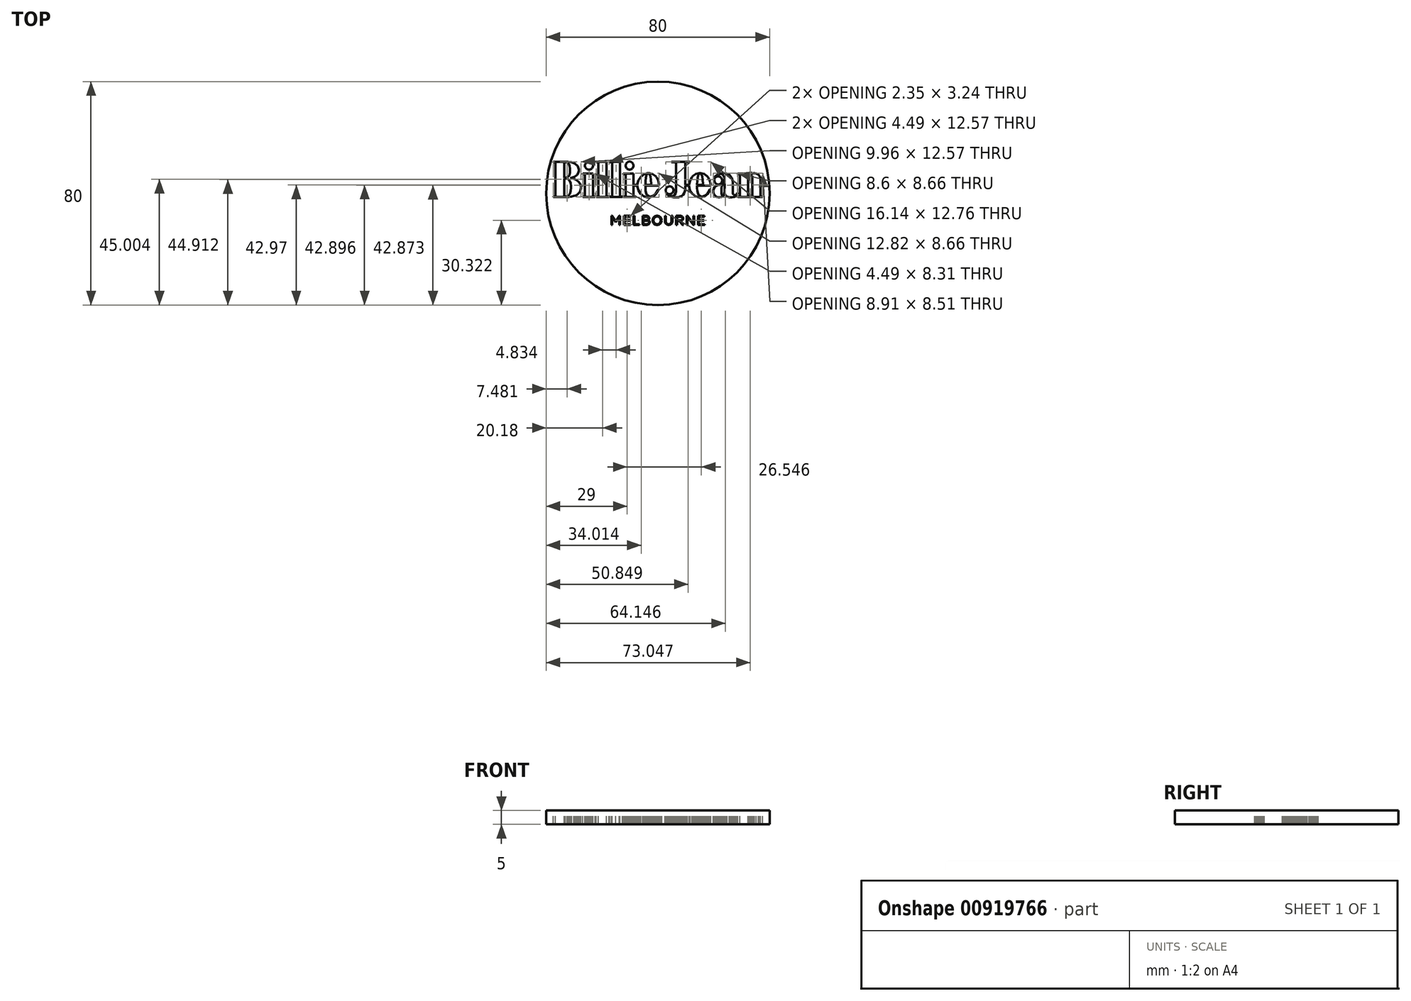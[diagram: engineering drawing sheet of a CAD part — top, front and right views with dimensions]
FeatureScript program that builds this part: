
annotation { "Feature Type Name" : "Feature", "Feature Type Description" : "" }
export const myFeature = defineFeature(function(context is Context, id is Id, definition is map)
    precondition{}
    {
        {
            var Q0;
            Q0=qCreatedBy(makeId("Top.planeOp"),FACE);
            var sketch = newSketch(context, id + "F0", { "sketchPlane" : qUnion([Q0])});
            skLineSegment(sketch, "E0.bottom", {"start": v(40, -20) * mm, "end": v(-40, -20) * mm});
            skLineSegment(sketch, "E0.top", {"start": v(40, 20) * mm, "end": v(-40, 20) * mm});
            skLineSegment(sketch, "E0.left", {"start": v(40, -20) * mm, "end": v(40, 20) * mm});
            skLineSegment(sketch, "E0.right", {"start": v(-40, -20) * mm, "end": v(-40, 20) * mm});
            skPoint(sketch, "E0.middle", {"position": v(0, 0) * mm});
            skCircle(sketch, "E1", {"center": v(0, 0) * mm, "radius": 40 * mm});
            skSolve(sketch);
        }
        {
            var Q0;
            Q0 = qSketchRegion(id + "F0", true);
            extrude(context, id + "F1", {"entities" : qUnion([Q0]), "depth" : 5 * mm, "offsetDistance" : 25 * mm});
        }
        {
            var Q0;
            Q0=makeQuery(id+"F1.opExtrude","CAP_FACE",FACE,{"disambiguationData":[OSD([sQuery(id+"F0.wireOp",EDGE,"E0.bottom"),sQuery(id+"F0.wireOp",EDGE,"E0.top"),sQuery(id+"F0.wireOp",EDGE,"E0.left"),sQuery(id+"F0.wireOp",EDGE,"E0.right")])],"isStart":false});
            var sketch = newSketch(context, id + "F2", { "sketchPlane" : qUnion([Q0])});
            skLineSegment(sketch, "E2", {"start": v(-15.09, -9.91) * mm, "end": v(-16.34, -8.06) * mm});
            skLineSegment(sketch, "E3", {"start": v(-16.34, -8.06) * mm, "end": v(-16.62, -8.06) * mm});
            skLineSegment(sketch, "E4", {"start": v(-16.62, -8.06) * mm, "end": v(-16.62, -11.3) * mm});
            skLineSegment(sketch, "E5", {"start": v(-16.62, -11.3) * mm, "end": v(-16.32, -11.3) * mm});
            skLineSegment(sketch, "E6", {"start": v(-16.32, -11.3) * mm, "end": v(-16.32, -8.61) * mm});
            skLineSegment(sketch, "E7", {"start": v(-16.32, -8.61) * mm, "end": v(-15.13, -10.36) * mm});
            skLineSegment(sketch, "E8", {"start": v(-15.13, -10.36) * mm, "end": v(-15.12, -10.37) * mm});
            skLineSegment(sketch, "E9", {"start": v(-15.12, -10.37) * mm, "end": v(-15.06, -10.37) * mm});
            skLineSegment(sketch, "E10", {"start": v(-15.06, -10.37) * mm, "end": v(-13.86, -8.61) * mm});
            skLineSegment(sketch, "E11", {"start": v(-13.86, -8.61) * mm, "end": v(-13.86, -11.3) * mm});
            skLineSegment(sketch, "E12", {"start": v(-13.86, -11.3) * mm, "end": v(-13.56, -11.3) * mm});
            skLineSegment(sketch, "E13", {"start": v(-13.56, -11.3) * mm, "end": v(-13.56, -8.06) * mm});
            skLineSegment(sketch, "E14", {"start": v(-13.56, -8.06) * mm, "end": v(-13.83, -8.06) * mm});
            skLineSegment(sketch, "E15", {"start": v(-13.83, -8.06) * mm, "end": v(-15.09, -9.91) * mm});
            skLineSegment(sketch, "E16", {"start": v(-11.87, -9.8) * mm, "end": v(-10.05, -9.8) * mm});
            skLineSegment(sketch, "E17", {"start": v(-10.05, -9.8) * mm, "end": v(-10.05, -9.52) * mm});
            skLineSegment(sketch, "E18", {"start": v(-10.05, -9.52) * mm, "end": v(-11.87, -9.52) * mm});
            skLineSegment(sketch, "E19", {"start": v(-11.87, -9.52) * mm, "end": v(-11.87, -8.34) * mm});
            skLineSegment(sketch, "E20", {"start": v(-11.87, -8.34) * mm, "end": v(-9.85, -8.34) * mm});
            skLineSegment(sketch, "E21", {"start": v(-9.85, -8.34) * mm, "end": v(-9.85, -8.06) * mm});
            skLineSegment(sketch, "E22", {"start": v(-9.85, -8.06) * mm, "end": v(-12.17, -8.06) * mm});
            skLineSegment(sketch, "E23", {"start": v(-12.17, -8.06) * mm, "end": v(-12.17, -11.3) * mm});
            skLineSegment(sketch, "E24", {"start": v(-12.17, -11.3) * mm, "end": v(-9.83, -11.3) * mm});
            skLineSegment(sketch, "E25", {"start": v(-9.83, -11.3) * mm, "end": v(-9.83, -11.02) * mm});
            skLineSegment(sketch, "E26", {"start": v(-9.83, -11.02) * mm, "end": v(-11.87, -11.02) * mm});
            skLineSegment(sketch, "E27", {"start": v(-11.87, -11.02) * mm, "end": v(-11.87, -9.8) * mm});
            skLineSegment(sketch, "E28", {"start": v(-8.43, -8.06) * mm, "end": v(-8.73, -8.06) * mm});
            skLineSegment(sketch, "E29", {"start": v(-8.73, -8.06) * mm, "end": v(-8.73, -11.3) * mm});
            skLineSegment(sketch, "E30", {"start": v(-8.73, -11.3) * mm, "end": v(-6.56, -11.3) * mm});
            skLineSegment(sketch, "E31", {"start": v(-6.56, -11.3) * mm, "end": v(-6.56, -11.02) * mm});
            skLineSegment(sketch, "E32", {"start": v(-6.56, -11.02) * mm, "end": v(-8.43, -11.02) * mm});
            skLineSegment(sketch, "E33", {"start": v(-8.43, -11.02) * mm, "end": v(-8.43, -8.06) * mm});
            skLineSegment(sketch, "E34", {"start": v(-5.2, -9.8) * mm, "end": v(-4.15, -9.8) * mm});
            skLineSegment(sketch, "E35", {"start": v(-4.15, -9.8) * mm, "end": v(-3.98, -9.8) * mm});
            skLineSegment(sketch, "E36", {"start": v(-3.98, -9.8) * mm, "end": v(-3.46, -9.96) * mm});
            skLineSegment(sketch, "E37", {"start": v(-3.46, -9.96) * mm, "end": v(-3.22, -10.28) * mm});
            skLineSegment(sketch, "E38", {"start": v(-3.22, -10.28) * mm, "end": v(-3.22, -10.4) * mm});
            skLineSegment(sketch, "E39", {"start": v(-3.22, -10.4) * mm, "end": v(-3.22, -10.4) * mm});
            skLineSegment(sketch, "E40", {"start": v(-3.22, -10.4) * mm, "end": v(-3.22, -10.51) * mm});
            skLineSegment(sketch, "E41", {"start": v(-3.22, -10.51) * mm, "end": v(-3.45, -10.85) * mm});
            skLineSegment(sketch, "E42", {"start": v(-3.45, -10.85) * mm, "end": v(-3.92, -11.02) * mm});
            skLineSegment(sketch, "E43", {"start": v(-3.92, -11.02) * mm, "end": v(-4.07, -11.02) * mm});
            skLineSegment(sketch, "E44", {"start": v(-4.07, -11.02) * mm, "end": v(-5.2, -11.02) * mm});
            skLineSegment(sketch, "E45", {"start": v(-5.2, -11.02) * mm, "end": v(-5.2, -9.8) * mm});
            skLineSegment(sketch, "E46", {"start": v(-4.15, -8.34) * mm, "end": v(-4.01, -8.34) * mm});
            skLineSegment(sketch, "E47", {"start": v(-4.01, -8.34) * mm, "end": v(-3.6, -8.49) * mm});
            skLineSegment(sketch, "E48", {"start": v(-3.6, -8.49) * mm, "end": v(-3.4, -8.8) * mm});
            skLineSegment(sketch, "E49", {"start": v(-3.4, -8.8) * mm, "end": v(-3.4, -8.9) * mm});
            skLineSegment(sketch, "E50", {"start": v(-3.4, -8.9) * mm, "end": v(-3.4, -8.9) * mm});
            skLineSegment(sketch, "E51", {"start": v(-3.4, -8.9) * mm, "end": v(-3.4, -9.02) * mm});
            skLineSegment(sketch, "E52", {"start": v(-3.4, -9.02) * mm, "end": v(-3.6, -9.36) * mm});
            skLineSegment(sketch, "E53", {"start": v(-3.6, -9.36) * mm, "end": v(-4.03, -9.52) * mm});
            skLineSegment(sketch, "E54", {"start": v(-4.03, -9.52) * mm, "end": v(-4.18, -9.52) * mm});
            skLineSegment(sketch, "E55", {"start": v(-4.18, -9.52) * mm, "end": v(-5.2, -9.52) * mm});
            skLineSegment(sketch, "E56", {"start": v(-5.2, -9.52) * mm, "end": v(-5.2, -8.34) * mm});
            skLineSegment(sketch, "E57", {"start": v(-5.2, -8.34) * mm, "end": v(-4.15, -8.34) * mm});
            skLineSegment(sketch, "E58", {"start": v(-3.56, -9.63) * mm, "end": v(-3.5, -9.6) * mm});
            skLineSegment(sketch, "E59", {"start": v(-3.5, -9.6) * mm, "end": v(-3.24, -9.36) * mm});
            skLineSegment(sketch, "E60", {"start": v(-3.24, -9.36) * mm, "end": v(-3.09, -9) * mm});
            skLineSegment(sketch, "E61", {"start": v(-3.09, -9) * mm, "end": v(-3.09, -8.88) * mm});
            skLineSegment(sketch, "E62", {"start": v(-3.09, -8.88) * mm, "end": v(-3.09, -8.87) * mm});
            skLineSegment(sketch, "E63", {"start": v(-3.09, -8.87) * mm, "end": v(-3.09, -8.72) * mm});
            skLineSegment(sketch, "E64", {"start": v(-3.09, -8.72) * mm, "end": v(-3.38, -8.28) * mm});
            skLineSegment(sketch, "E65", {"start": v(-3.38, -8.28) * mm, "end": v(-3.96, -8.06) * mm});
            skLineSegment(sketch, "E66", {"start": v(-3.96, -8.06) * mm, "end": v(-4.15, -8.06) * mm});
            skLineSegment(sketch, "E67", {"start": v(-4.15, -8.06) * mm, "end": v(-5.5, -8.06) * mm});
            skLineSegment(sketch, "E68", {"start": v(-5.5, -8.06) * mm, "end": v(-5.5, -11.3) * mm});
            skLineSegment(sketch, "E69", {"start": v(-5.5, -11.3) * mm, "end": v(-4.08, -11.3) * mm});
            skLineSegment(sketch, "E70", {"start": v(-4.08, -11.3) * mm, "end": v(-3.87, -11.3) * mm});
            skLineSegment(sketch, "E71", {"start": v(-3.87, -11.3) * mm, "end": v(-3.23, -11.05) * mm});
            skLineSegment(sketch, "E72", {"start": v(-3.23, -11.05) * mm, "end": v(-2.9, -10.56) * mm});
            skLineSegment(sketch, "E73", {"start": v(-2.9, -10.56) * mm, "end": v(-2.9, -10.4) * mm});
            skLineSegment(sketch, "E74", {"start": v(-2.9, -10.4) * mm, "end": v(-2.9, -10.4) * mm});
            skLineSegment(sketch, "E75", {"start": v(-2.9, -10.4) * mm, "end": v(-2.9, -10.27) * mm});
            skLineSegment(sketch, "E76", {"start": v(-2.9, -10.27) * mm, "end": v(-3.08, -9.92) * mm});
            skLineSegment(sketch, "E77", {"start": v(-3.08, -9.92) * mm, "end": v(-3.46, -9.66) * mm});
            skLineSegment(sketch, "E78", {"start": v(-3.46, -9.66) * mm, "end": v(-3.56, -9.63) * mm});
            skLineSegment(sketch, "E79", {"start": v(-0.28, -11.07) * mm, "end": v(-0.4, -11.07) * mm});
            skLineSegment(sketch, "E80", {"start": v(-0.4, -11.07) * mm, "end": v(-0.8, -10.97) * mm});
            skLineSegment(sketch, "E81", {"start": v(-0.8, -10.97) * mm, "end": v(-1.22, -10.67) * mm});
            skLineSegment(sketch, "E82", {"start": v(-1.22, -10.67) * mm, "end": v(-1.5, -10.23) * mm});
            skLineSegment(sketch, "E83", {"start": v(-1.5, -10.23) * mm, "end": v(-1.6, -9.81) * mm});
            skLineSegment(sketch, "E84", {"start": v(-1.6, -9.81) * mm, "end": v(-1.6, -9.68) * mm});
            skLineSegment(sketch, "E85", {"start": v(-1.6, -9.68) * mm, "end": v(-1.6, -9.67) * mm});
            skLineSegment(sketch, "E86", {"start": v(-1.6, -9.67) * mm, "end": v(-1.6, -9.53) * mm});
            skLineSegment(sketch, "E87", {"start": v(-1.6, -9.53) * mm, "end": v(-1.5, -9.12) * mm});
            skLineSegment(sketch, "E88", {"start": v(-1.5, -9.12) * mm, "end": v(-1.22, -8.68) * mm});
            skLineSegment(sketch, "E89", {"start": v(-1.22, -8.68) * mm, "end": v(-0.8, -8.39) * mm});
            skLineSegment(sketch, "E90", {"start": v(-0.8, -8.39) * mm, "end": v(-0.42, -8.28) * mm});
            skLineSegment(sketch, "E91", {"start": v(-0.42, -8.28) * mm, "end": v(-0.29, -8.28) * mm});
            skLineSegment(sketch, "E92", {"start": v(-0.29, -8.28) * mm, "end": v(-0.16, -8.28) * mm});
            skLineSegment(sketch, "E93", {"start": v(-0.16, -8.28) * mm, "end": v(0.23, -8.39) * mm});
            skLineSegment(sketch, "E94", {"start": v(0.23, -8.39) * mm, "end": v(0.65, -8.69) * mm});
            skLineSegment(sketch, "E95", {"start": v(0.65, -8.69) * mm, "end": v(0.93, -9.13) * mm});
            skLineSegment(sketch, "E96", {"start": v(0.93, -9.13) * mm, "end": v(1.04, -9.54) * mm});
            skLineSegment(sketch, "E97", {"start": v(1.04, -9.54) * mm, "end": v(1.04, -9.68) * mm});
            skLineSegment(sketch, "E98", {"start": v(1.04, -9.68) * mm, "end": v(1.04, -9.69) * mm});
            skLineSegment(sketch, "E99", {"start": v(1.04, -9.69) * mm, "end": v(1.04, -9.82) * mm});
            skLineSegment(sketch, "E100", {"start": v(1.04, -9.82) * mm, "end": v(0.94, -10.24) * mm});
            skLineSegment(sketch, "E101", {"start": v(0.94, -10.24) * mm, "end": v(0.66, -10.68) * mm});
            skLineSegment(sketch, "E102", {"start": v(0.66, -10.68) * mm, "end": v(0.24, -10.97) * mm});
            skLineSegment(sketch, "E103", {"start": v(0.24, -10.97) * mm, "end": v(-0.15, -11.07) * mm});
            skLineSegment(sketch, "E104", {"start": v(-0.15, -11.07) * mm, "end": v(-0.28, -11.07) * mm});
            skLineSegment(sketch, "E105", {"start": v(1.35, -9.66) * mm, "end": v(1.35, -9.5) * mm});
            skLineSegment(sketch, "E106", {"start": v(1.35, -9.5) * mm, "end": v(1.22, -9) * mm});
            skLineSegment(sketch, "E107", {"start": v(1.22, -9) * mm, "end": v(0.88, -8.47) * mm});
            skLineSegment(sketch, "E108", {"start": v(0.88, -8.47) * mm, "end": v(0.36, -8.13) * mm});
            skLineSegment(sketch, "E109", {"start": v(0.36, -8.13) * mm, "end": v(-0.12, -8) * mm});
            skLineSegment(sketch, "E110", {"start": v(-0.12, -8) * mm, "end": v(-0.28, -8) * mm});
            skLineSegment(sketch, "E111", {"start": v(-0.28, -8) * mm, "end": v(-0.45, -8) * mm});
            skLineSegment(sketch, "E112", {"start": v(-0.45, -8) * mm, "end": v(-0.96, -8.15) * mm});
            skLineSegment(sketch, "E113", {"start": v(-0.96, -8.15) * mm, "end": v(-1.48, -8.53) * mm});
            skLineSegment(sketch, "E114", {"start": v(-1.48, -8.53) * mm, "end": v(-1.8, -9.07) * mm});
            skLineSegment(sketch, "E115", {"start": v(-1.8, -9.07) * mm, "end": v(-1.91, -9.52) * mm});
            skLineSegment(sketch, "E116", {"start": v(-1.91, -9.52) * mm, "end": v(-1.91, -9.68) * mm});
            skLineSegment(sketch, "E117", {"start": v(-1.91, -9.68) * mm, "end": v(-1.91, -9.69) * mm});
            skLineSegment(sketch, "E118", {"start": v(-1.91, -9.69) * mm, "end": v(-1.91, -9.85) * mm});
            skLineSegment(sketch, "E119", {"start": v(-1.91, -9.85) * mm, "end": v(-1.79, -10.35) * mm});
            skLineSegment(sketch, "E120", {"start": v(-1.79, -10.35) * mm, "end": v(-1.45, -10.88) * mm});
            skLineSegment(sketch, "E121", {"start": v(-1.45, -10.88) * mm, "end": v(-0.93, -11.23) * mm});
            skLineSegment(sketch, "E122", {"start": v(-0.93, -11.23) * mm, "end": v(-0.45, -11.35) * mm});
            skLineSegment(sketch, "E123", {"start": v(-0.45, -11.35) * mm, "end": v(-0.29, -11.35) * mm});
            skLineSegment(sketch, "E124", {"start": v(-0.29, -11.35) * mm, "end": v(-0.12, -11.35) * mm});
            skLineSegment(sketch, "E125", {"start": v(-0.12, -11.35) * mm, "end": v(0.4, -11.2) * mm});
            skLineSegment(sketch, "E126", {"start": v(0.4, -11.2) * mm, "end": v(0.91, -10.83) * mm});
            skLineSegment(sketch, "E127", {"start": v(0.91, -10.83) * mm, "end": v(1.23, -10.3) * mm});
            skLineSegment(sketch, "E128", {"start": v(1.23, -10.3) * mm, "end": v(1.35, -9.84) * mm});
            skLineSegment(sketch, "E129", {"start": v(1.35, -9.84) * mm, "end": v(1.35, -9.7) * mm});
            skLineSegment(sketch, "E130", {"start": v(1.35, -9.7) * mm, "end": v(1.35, -9.69) * mm});
            skLineSegment(sketch, "E131", {"start": v(1.35, -9.69) * mm, "end": v(1.35, -9.68) * mm});
            skLineSegment(sketch, "E132", {"start": v(1.35, -9.68) * mm, "end": v(1.35, -9.67) * mm});
            skLineSegment(sketch, "E133", {"start": v(1.35, -9.67) * mm, "end": v(1.35, -9.66) * mm});
            skLineSegment(sketch, "E134", {"start": v(4.89, -9.95) * mm, "end": v(4.89, -10.15) * mm});
            skLineSegment(sketch, "E135", {"start": v(4.89, -10.15) * mm, "end": v(4.62, -10.78) * mm});
            skLineSegment(sketch, "E136", {"start": v(4.62, -10.78) * mm, "end": v(4.05, -11.07) * mm});
            skLineSegment(sketch, "E137", {"start": v(4.05, -11.07) * mm, "end": v(3.86, -11.07) * mm});
            skLineSegment(sketch, "E138", {"start": v(3.86, -11.07) * mm, "end": v(3.67, -11.07) * mm});
            skLineSegment(sketch, "E139", {"start": v(3.67, -11.07) * mm, "end": v(3.1, -10.77) * mm});
            skLineSegment(sketch, "E140", {"start": v(3.1, -10.77) * mm, "end": v(2.82, -10.14) * mm});
            skLineSegment(sketch, "E141", {"start": v(2.82, -10.14) * mm, "end": v(2.82, -9.92) * mm});
            skLineSegment(sketch, "E142", {"start": v(2.82, -9.92) * mm, "end": v(2.82, -8.06) * mm});
            skLineSegment(sketch, "E143", {"start": v(2.82, -8.06) * mm, "end": v(2.52, -8.06) * mm});
            skLineSegment(sketch, "E144", {"start": v(2.52, -8.06) * mm, "end": v(2.52, -9.95) * mm});
            skLineSegment(sketch, "E145", {"start": v(2.52, -9.95) * mm, "end": v(2.52, -10.1) * mm});
            skLineSegment(sketch, "E146", {"start": v(2.52, -10.1) * mm, "end": v(2.6, -10.53) * mm});
            skLineSegment(sketch, "E147", {"start": v(2.6, -10.53) * mm, "end": v(2.88, -10.97) * mm});
            skLineSegment(sketch, "E148", {"start": v(2.88, -10.97) * mm, "end": v(3.3, -11.25) * mm});
            skLineSegment(sketch, "E149", {"start": v(3.3, -11.25) * mm, "end": v(3.71, -11.35) * mm});
            skLineSegment(sketch, "E150", {"start": v(3.71, -11.35) * mm, "end": v(3.85, -11.35) * mm});
            skLineSegment(sketch, "E151", {"start": v(3.85, -11.35) * mm, "end": v(4, -11.35) * mm});
            skLineSegment(sketch, "E152", {"start": v(4, -11.35) * mm, "end": v(4.4, -11.25) * mm});
            skLineSegment(sketch, "E153", {"start": v(4.4, -11.25) * mm, "end": v(4.83, -10.96) * mm});
            skLineSegment(sketch, "E154", {"start": v(4.83, -10.96) * mm, "end": v(5.1, -10.51) * mm});
            skLineSegment(sketch, "E155", {"start": v(5.1, -10.51) * mm, "end": v(5.19, -10.07) * mm});
            skLineSegment(sketch, "E156", {"start": v(5.19, -10.07) * mm, "end": v(5.19, -9.92) * mm});
            skLineSegment(sketch, "E157", {"start": v(5.19, -9.92) * mm, "end": v(5.19, -8.06) * mm});
            skLineSegment(sketch, "E158", {"start": v(5.19, -8.06) * mm, "end": v(4.89, -8.06) * mm});
            skLineSegment(sketch, "E159", {"start": v(4.89, -8.06) * mm, "end": v(4.89, -9.95) * mm});
            skLineSegment(sketch, "E160", {"start": v(6.83, -8.34) * mm, "end": v(7.88, -8.34) * mm});
            skLineSegment(sketch, "E161", {"start": v(7.88, -8.34) * mm, "end": v(8.05, -8.34) * mm});
            skLineSegment(sketch, "E162", {"start": v(8.05, -8.34) * mm, "end": v(8.53, -8.52) * mm});
            skLineSegment(sketch, "E163", {"start": v(8.53, -8.52) * mm, "end": v(8.76, -8.88) * mm});
            skLineSegment(sketch, "E164", {"start": v(8.76, -8.88) * mm, "end": v(8.76, -9) * mm});
            skLineSegment(sketch, "E165", {"start": v(8.76, -9) * mm, "end": v(8.76, -9.01) * mm});
            skLineSegment(sketch, "E166", {"start": v(8.76, -9.01) * mm, "end": v(8.76, -9.14) * mm});
            skLineSegment(sketch, "E167", {"start": v(8.76, -9.14) * mm, "end": v(8.52, -9.52) * mm});
            skLineSegment(sketch, "E168", {"start": v(8.52, -9.52) * mm, "end": v(8.03, -9.7) * mm});
            skLineSegment(sketch, "E169", {"start": v(8.03, -9.7) * mm, "end": v(7.87, -9.7) * mm});
            skLineSegment(sketch, "E170", {"start": v(7.87, -9.7) * mm, "end": v(6.83, -9.7) * mm});
            skLineSegment(sketch, "E171", {"start": v(6.83, -9.7) * mm, "end": v(6.83, -8.34) * mm});
            skLineSegment(sketch, "E172", {"start": v(9.07, -9) * mm, "end": v(9.07, -9) * mm});
            skLineSegment(sketch, "E173", {"start": v(9.07, -9) * mm, "end": v(9.07, -8.82) * mm});
            skLineSegment(sketch, "E174", {"start": v(9.07, -8.82) * mm, "end": v(8.74, -8.31) * mm});
            skLineSegment(sketch, "E175", {"start": v(8.74, -8.31) * mm, "end": v(8.11, -8.06) * mm});
            skLineSegment(sketch, "E176", {"start": v(8.11, -8.06) * mm, "end": v(7.9, -8.06) * mm});
            skLineSegment(sketch, "E177", {"start": v(7.9, -8.06) * mm, "end": v(6.53, -8.06) * mm});
            skLineSegment(sketch, "E178", {"start": v(6.53, -8.06) * mm, "end": v(6.53, -11.3) * mm});
            skLineSegment(sketch, "E179", {"start": v(6.53, -11.3) * mm, "end": v(6.83, -11.3) * mm});
            skLineSegment(sketch, "E180", {"start": v(6.83, -11.3) * mm, "end": v(6.83, -9.98) * mm});
            skLineSegment(sketch, "E181", {"start": v(6.83, -9.98) * mm, "end": v(7.82, -9.98) * mm});
            skLineSegment(sketch, "E182", {"start": v(7.82, -9.98) * mm, "end": v(8.83, -11.3) * mm});
            skLineSegment(sketch, "E183", {"start": v(8.83, -11.3) * mm, "end": v(9.22, -11.3) * mm});
            skLineSegment(sketch, "E184", {"start": v(9.22, -11.3) * mm, "end": v(8.16, -9.93) * mm});
            skLineSegment(sketch, "E185", {"start": v(8.16, -9.93) * mm, "end": v(8.3, -9.91) * mm});
            skLineSegment(sketch, "E186", {"start": v(8.3, -9.91) * mm, "end": v(8.83, -9.62) * mm});
            skLineSegment(sketch, "E187", {"start": v(8.83, -9.62) * mm, "end": v(9.07, -9.16) * mm});
            skLineSegment(sketch, "E188", {"start": v(9.07, -9.16) * mm, "end": v(9.07, -9) * mm});
            skLineSegment(sketch, "E189", {"start": v(12.7, -10.76) * mm, "end": v(10.57, -8.07) * mm});
            skLineSegment(sketch, "E190", {"start": v(10.57, -8.07) * mm, "end": v(10.56, -8.06) * mm});
            skLineSegment(sketch, "E191", {"start": v(10.56, -8.06) * mm, "end": v(10.29, -8.06) * mm});
            skLineSegment(sketch, "E192", {"start": v(10.29, -8.06) * mm, "end": v(10.29, -11.3) * mm});
            skLineSegment(sketch, "E193", {"start": v(10.29, -11.3) * mm, "end": v(10.58, -11.3) * mm});
            skLineSegment(sketch, "E194", {"start": v(10.58, -11.3) * mm, "end": v(10.58, -8.54) * mm});
            skLineSegment(sketch, "E195", {"start": v(10.58, -8.54) * mm, "end": v(12.76, -11.29) * mm});
            skLineSegment(sketch, "E196", {"start": v(12.76, -11.29) * mm, "end": v(12.77, -11.3) * mm});
            skLineSegment(sketch, "E197", {"start": v(12.77, -11.3) * mm, "end": v(13, -11.3) * mm});
            skLineSegment(sketch, "E198", {"start": v(13, -11.3) * mm, "end": v(13, -8.06) * mm});
            skLineSegment(sketch, "E199", {"start": v(13, -8.06) * mm, "end": v(12.7, -8.06) * mm});
            skLineSegment(sketch, "E200", {"start": v(12.7, -8.06) * mm, "end": v(12.7, -10.76) * mm});
            skLineSegment(sketch, "E201", {"start": v(14.67, -11.02) * mm, "end": v(14.67, -9.8) * mm});
            skLineSegment(sketch, "E202", {"start": v(14.67, -9.8) * mm, "end": v(16.5, -9.8) * mm});
            skLineSegment(sketch, "E203", {"start": v(16.5, -9.8) * mm, "end": v(16.5, -9.52) * mm});
            skLineSegment(sketch, "E204", {"start": v(16.5, -9.52) * mm, "end": v(14.67, -9.52) * mm});
            skLineSegment(sketch, "E205", {"start": v(14.67, -9.52) * mm, "end": v(14.67, -8.34) * mm});
            skLineSegment(sketch, "E206", {"start": v(14.67, -8.34) * mm, "end": v(16.7, -8.34) * mm});
            skLineSegment(sketch, "E207", {"start": v(16.7, -8.34) * mm, "end": v(16.7, -8.06) * mm});
            skLineSegment(sketch, "E208", {"start": v(16.7, -8.06) * mm, "end": v(14.37, -8.06) * mm});
            skLineSegment(sketch, "E209", {"start": v(14.37, -8.06) * mm, "end": v(14.37, -11.3) * mm});
            skLineSegment(sketch, "E210", {"start": v(14.37, -11.3) * mm, "end": v(16.72, -11.3) * mm});
            skLineSegment(sketch, "E211", {"start": v(16.72, -11.3) * mm, "end": v(16.72, -11.02) * mm});
            skLineSegment(sketch, "E212", {"start": v(16.72, -11.02) * mm, "end": v(14.67, -11.02) * mm});
            skLineSegment(sketch, "E213", {"start": v(-24.66, 11.35) * mm, "end": v(-24.8, 11.35) * mm});
            skLineSegment(sketch, "E214", {"start": v(-24.8, 11.35) * mm, "end": v(-25.21, 11.24) * mm});
            skLineSegment(sketch, "E215", {"start": v(-25.21, 11.24) * mm, "end": v(-25.67, 10.93) * mm});
            skLineSegment(sketch, "E216", {"start": v(-25.67, 10.93) * mm, "end": v(-25.98, 10.48) * mm});
            skLineSegment(sketch, "E217", {"start": v(-25.98, 10.48) * mm, "end": v(-26.1, 10.06) * mm});
            skLineSegment(sketch, "E218", {"start": v(-26.1, 10.06) * mm, "end": v(-26.1, 9.92) * mm});
            skLineSegment(sketch, "E219", {"start": v(-26.1, 9.92) * mm, "end": v(-26.1, 9.78) * mm});
            skLineSegment(sketch, "E220", {"start": v(-26.1, 9.78) * mm, "end": v(-25.98, 9.36) * mm});
            skLineSegment(sketch, "E221", {"start": v(-25.98, 9.36) * mm, "end": v(-25.67, 8.9) * mm});
            skLineSegment(sketch, "E222", {"start": v(-25.67, 8.9) * mm, "end": v(-25.21, 8.6) * mm});
            skLineSegment(sketch, "E223", {"start": v(-25.21, 8.6) * mm, "end": v(-24.8, 8.48) * mm});
            skLineSegment(sketch, "E224", {"start": v(-24.8, 8.48) * mm, "end": v(-24.66, 8.48) * mm});
            skLineSegment(sketch, "E225", {"start": v(-24.66, 8.48) * mm, "end": v(-24.52, 8.48) * mm});
            skLineSegment(sketch, "E226", {"start": v(-24.52, 8.48) * mm, "end": v(-24.1, 8.6) * mm});
            skLineSegment(sketch, "E227", {"start": v(-24.1, 8.6) * mm, "end": v(-23.64, 8.9) * mm});
            skLineSegment(sketch, "E228", {"start": v(-23.64, 8.9) * mm, "end": v(-23.33, 9.36) * mm});
            skLineSegment(sketch, "E229", {"start": v(-23.33, 9.36) * mm, "end": v(-23.22, 9.78) * mm});
            skLineSegment(sketch, "E230", {"start": v(-23.22, 9.78) * mm, "end": v(-23.22, 9.92) * mm});
            skLineSegment(sketch, "E231", {"start": v(-23.22, 9.92) * mm, "end": v(-23.22, 10.06) * mm});
            skLineSegment(sketch, "E232", {"start": v(-23.22, 10.06) * mm, "end": v(-23.33, 10.48) * mm});
            skLineSegment(sketch, "E233", {"start": v(-23.33, 10.48) * mm, "end": v(-23.64, 10.93) * mm});
            skLineSegment(sketch, "E234", {"start": v(-23.64, 10.93) * mm, "end": v(-24.1, 11.24) * mm});
            skLineSegment(sketch, "E235", {"start": v(-24.1, 11.24) * mm, "end": v(-24.52, 11.35) * mm});
            skLineSegment(sketch, "E236", {"start": v(-24.52, 11.35) * mm, "end": v(-24.66, 11.35) * mm});
            skLineSegment(sketch, "E237", {"start": v(-10.15, 11.35) * mm, "end": v(-10.3, 11.35) * mm});
            skLineSegment(sketch, "E238", {"start": v(-10.3, 11.35) * mm, "end": v(-10.71, 11.24) * mm});
            skLineSegment(sketch, "E239", {"start": v(-10.71, 11.24) * mm, "end": v(-11.17, 10.93) * mm});
            skLineSegment(sketch, "E240", {"start": v(-11.17, 10.93) * mm, "end": v(-11.48, 10.48) * mm});
            skLineSegment(sketch, "E241", {"start": v(-11.48, 10.48) * mm, "end": v(-11.59, 10.06) * mm});
            skLineSegment(sketch, "E242", {"start": v(-11.59, 10.06) * mm, "end": v(-11.59, 9.92) * mm});
            skLineSegment(sketch, "E243", {"start": v(-11.59, 9.92) * mm, "end": v(-11.59, 9.78) * mm});
            skLineSegment(sketch, "E244", {"start": v(-11.59, 9.78) * mm, "end": v(-11.48, 9.36) * mm});
            skLineSegment(sketch, "E245", {"start": v(-11.48, 9.36) * mm, "end": v(-11.17, 8.9) * mm});
            skLineSegment(sketch, "E246", {"start": v(-11.17, 8.9) * mm, "end": v(-10.71, 8.6) * mm});
            skLineSegment(sketch, "E247", {"start": v(-10.71, 8.6) * mm, "end": v(-10.3, 8.48) * mm});
            skLineSegment(sketch, "E248", {"start": v(-10.3, 8.48) * mm, "end": v(-10.15, 8.48) * mm});
            skLineSegment(sketch, "E249", {"start": v(-10.15, 8.48) * mm, "end": v(-10.01, 8.48) * mm});
            skLineSegment(sketch, "E250", {"start": v(-10.01, 8.48) * mm, "end": v(-9.6, 8.6) * mm});
            skLineSegment(sketch, "E251", {"start": v(-9.6, 8.6) * mm, "end": v(-9.14, 8.9) * mm});
            skLineSegment(sketch, "E252", {"start": v(-9.14, 8.9) * mm, "end": v(-8.83, 9.36) * mm});
            skLineSegment(sketch, "E253", {"start": v(-8.83, 9.36) * mm, "end": v(-8.72, 9.78) * mm});
            skLineSegment(sketch, "E254", {"start": v(-8.72, 9.78) * mm, "end": v(-8.72, 9.92) * mm});
            skLineSegment(sketch, "E255", {"start": v(-8.72, 9.92) * mm, "end": v(-8.72, 10.06) * mm});
            skLineSegment(sketch, "E256", {"start": v(-8.72, 10.06) * mm, "end": v(-8.83, 10.48) * mm});
            skLineSegment(sketch, "E257", {"start": v(-8.83, 10.48) * mm, "end": v(-9.14, 10.93) * mm});
            skLineSegment(sketch, "E258", {"start": v(-9.14, 10.93) * mm, "end": v(-9.6, 11.24) * mm});
            skLineSegment(sketch, "E259", {"start": v(-9.6, 11.24) * mm, "end": v(-10.01, 11.35) * mm});
            skLineSegment(sketch, "E260", {"start": v(-10.01, 11.35) * mm, "end": v(-10.15, 11.35) * mm});
            skLineSegment(sketch, "E261", {"start": v(-33.47, 5.51) * mm, "end": v(-33.47, 11.14) * mm});
            skLineSegment(sketch, "E262", {"start": v(-33.47, 11.14) * mm, "end": v(-33.24, 11.14) * mm});
            skLineSegment(sketch, "E263", {"start": v(-33.24, 11.14) * mm, "end": v(-32.55, 10.98) * mm});
            skLineSegment(sketch, "E264", {"start": v(-32.55, 10.98) * mm, "end": v(-31.91, 10.5) * mm});
            skLineSegment(sketch, "E265", {"start": v(-31.91, 10.5) * mm, "end": v(-31.55, 9.7) * mm});
            skLineSegment(sketch, "E266", {"start": v(-31.55, 9.7) * mm, "end": v(-31.43, 8.82) * mm});
            skLineSegment(sketch, "E267", {"start": v(-31.43, 8.82) * mm, "end": v(-31.43, 8.53) * mm});
            skLineSegment(sketch, "E268", {"start": v(-31.43, 8.53) * mm, "end": v(-31.43, 8.22) * mm});
            skLineSegment(sketch, "E269", {"start": v(-31.43, 8.22) * mm, "end": v(-31.48, 7.29) * mm});
            skLineSegment(sketch, "E270", {"start": v(-31.48, 7.29) * mm, "end": v(-31.72, 6.36) * mm});
            skLineSegment(sketch, "E271", {"start": v(-31.72, 6.36) * mm, "end": v(-32.33, 5.76) * mm});
            skLineSegment(sketch, "E272", {"start": v(-32.33, 5.76) * mm, "end": v(-33.19, 5.53) * mm});
            skLineSegment(sketch, "E273", {"start": v(-33.19, 5.53) * mm, "end": v(-33.47, 5.51) * mm});
            skLineSegment(sketch, "E274", {"start": v(-33.47, 5.35) * mm, "end": v(-33.17, 5.35) * mm});
            skLineSegment(sketch, "E275", {"start": v(-33.17, 5.35) * mm, "end": v(-32.27, 5.15) * mm});
            skLineSegment(sketch, "E276", {"start": v(-32.27, 5.15) * mm, "end": v(-31.55, 4.57) * mm});
            skLineSegment(sketch, "E277", {"start": v(-31.55, 4.57) * mm, "end": v(-31.2, 3.63) * mm});
            skLineSegment(sketch, "E278", {"start": v(-31.2, 3.63) * mm, "end": v(-31.11, 2.67) * mm});
            skLineSegment(sketch, "E279", {"start": v(-31.11, 2.67) * mm, "end": v(-31.11, 2.35) * mm});
            skLineSegment(sketch, "E280", {"start": v(-31.11, 2.35) * mm, "end": v(-31.11, 2) * mm});
            skLineSegment(sketch, "E281", {"start": v(-31.11, 2) * mm, "end": v(-31.17, 0.9) * mm});
            skLineSegment(sketch, "E282", {"start": v(-31.17, 0.9) * mm, "end": v(-31.47, -0.18) * mm});
            skLineSegment(sketch, "E283", {"start": v(-31.47, -0.18) * mm, "end": v(-32.18, -0.87) * mm});
            skLineSegment(sketch, "E284", {"start": v(-32.18, -0.87) * mm, "end": v(-33.15, -1.12) * mm});
            skLineSegment(sketch, "E285", {"start": v(-33.15, -1.12) * mm, "end": v(-33.47, -1.12) * mm});
            skLineSegment(sketch, "E286", {"start": v(-33.47, -1.12) * mm, "end": v(-33.47, 5.35) * mm});
            skLineSegment(sketch, "E287", {"start": v(-31.3, 5.45) * mm, "end": v(-30.91, 5.5) * mm});
            skLineSegment(sketch, "E288", {"start": v(-30.91, 5.5) * mm, "end": v(-29.79, 5.9) * mm});
            skLineSegment(sketch, "E289", {"start": v(-29.79, 5.9) * mm, "end": v(-28.87, 6.61) * mm});
            skLineSegment(sketch, "E290", {"start": v(-28.87, 6.61) * mm, "end": v(-28.42, 7.46) * mm});
            skLineSegment(sketch, "E291", {"start": v(-28.42, 7.46) * mm, "end": v(-28.3, 8.1) * mm});
            skLineSegment(sketch, "E292", {"start": v(-28.3, 8.1) * mm, "end": v(-28.3, 8.32) * mm});
            skLineSegment(sketch, "E293", {"start": v(-28.3, 8.32) * mm, "end": v(-28.3, 8.67) * mm});
            skLineSegment(sketch, "E294", {"start": v(-28.3, 8.67) * mm, "end": v(-28.67, 9.7) * mm});
            skLineSegment(sketch, "E295", {"start": v(-28.67, 9.7) * mm, "end": v(-29.65, 10.63) * mm});
            skLineSegment(sketch, "E296", {"start": v(-29.65, 10.63) * mm, "end": v(-31.01, 11.14) * mm});
            skLineSegment(sketch, "E297", {"start": v(-31.01, 11.14) * mm, "end": v(-32.16, 11.3) * mm});
            skLineSegment(sketch, "E298", {"start": v(-32.16, 11.3) * mm, "end": v(-32.54, 11.3) * mm});
            skLineSegment(sketch, "E299", {"start": v(-32.54, 11.3) * mm, "end": v(-37.5, 11.3) * mm});
            skLineSegment(sketch, "E300", {"start": v(-37.5, 11.3) * mm, "end": v(-37.5, 11.14) * mm});
            skLineSegment(sketch, "E301", {"start": v(-37.5, 11.14) * mm, "end": v(-36.7, 11.14) * mm});
            skLineSegment(sketch, "E302", {"start": v(-36.7, 11.14) * mm, "end": v(-36.7, -1.13) * mm});
            skLineSegment(sketch, "E303", {"start": v(-36.7, -1.13) * mm, "end": v(-37.5, -1.13) * mm});
            skLineSegment(sketch, "E304", {"start": v(-37.5, -1.13) * mm, "end": v(-37.5, -1.28) * mm});
            skLineSegment(sketch, "E305", {"start": v(-37.5, -1.28) * mm, "end": v(-32.4, -1.28) * mm});
            skLineSegment(sketch, "E306", {"start": v(-32.4, -1.28) * mm, "end": v(-32.24, -1.28) * mm});
            skLineSegment(sketch, "E307", {"start": v(-32.24, -1.28) * mm, "end": v(-31.77, -1.26) * mm});
            skLineSegment(sketch, "E308", {"start": v(-31.77, -1.26) * mm, "end": v(-30.98, -1.17) * mm});
            skLineSegment(sketch, "E309", {"start": v(-30.98, -1.17) * mm, "end": v(-30.12, -0.97) * mm});
            skLineSegment(sketch, "E310", {"start": v(-30.12, -0.97) * mm, "end": v(-29.46, -0.73) * mm});
            skLineSegment(sketch, "E311", {"start": v(-29.46, -0.73) * mm, "end": v(-29.26, -0.62) * mm});
            skLineSegment(sketch, "E312", {"start": v(-29.26, -0.62) * mm, "end": v(-28.97, -0.48) * mm});
            skLineSegment(sketch, "E313", {"start": v(-28.97, -0.48) * mm, "end": v(-27.97, 0.5) * mm});
            skLineSegment(sketch, "E314", {"start": v(-27.97, 0.5) * mm, "end": v(-27.54, 1.71) * mm});
            skLineSegment(sketch, "E315", {"start": v(-27.54, 1.71) * mm, "end": v(-27.54, 2.11) * mm});
            skLineSegment(sketch, "E316", {"start": v(-27.54, 2.11) * mm, "end": v(-27.54, 2.43) * mm});
            skLineSegment(sketch, "E317", {"start": v(-27.54, 2.43) * mm, "end": v(-27.78, 3.37) * mm});
            skLineSegment(sketch, "E318", {"start": v(-27.78, 3.37) * mm, "end": v(-28.5, 4.36) * mm});
            skLineSegment(sketch, "E319", {"start": v(-28.5, 4.36) * mm, "end": v(-29.69, 5.06) * mm});
            skLineSegment(sketch, "E320", {"start": v(-29.69, 5.06) * mm, "end": v(-30.9, 5.4) * mm});
            skLineSegment(sketch, "E321", {"start": v(-30.9, 5.4) * mm, "end": v(-31.3, 5.45) * mm});
            skLineSegment(sketch, "E322", {"start": v(-23.22, 7.03) * mm, "end": v(-26.9, 7.03) * mm});
            skLineSegment(sketch, "E323", {"start": v(-26.9, 7.03) * mm, "end": v(-26.9, 6.88) * mm});
            skLineSegment(sketch, "E324", {"start": v(-26.9, 6.88) * mm, "end": v(-26.1, 6.88) * mm});
            skLineSegment(sketch, "E325", {"start": v(-26.1, 6.88) * mm, "end": v(-26.1, -1.13) * mm});
            skLineSegment(sketch, "E326", {"start": v(-26.1, -1.13) * mm, "end": v(-26.9, -1.13) * mm});
            skLineSegment(sketch, "E327", {"start": v(-26.9, -1.13) * mm, "end": v(-26.9, -1.28) * mm});
            skLineSegment(sketch, "E328", {"start": v(-26.9, -1.28) * mm, "end": v(-22.4, -1.28) * mm});
            skLineSegment(sketch, "E329", {"start": v(-22.4, -1.28) * mm, "end": v(-22.4, -1.13) * mm});
            skLineSegment(sketch, "E330", {"start": v(-22.4, -1.13) * mm, "end": v(-23.22, -1.13) * mm});
            skLineSegment(sketch, "E331", {"start": v(-23.22, -1.13) * mm, "end": v(-23.22, 7.03) * mm});
            skLineSegment(sketch, "E332", {"start": v(-18.39, 11.3) * mm, "end": v(-22.07, 11.3) * mm});
            skLineSegment(sketch, "E333", {"start": v(-22.07, 11.3) * mm, "end": v(-22.07, 11.14) * mm});
            skLineSegment(sketch, "E334", {"start": v(-22.07, 11.14) * mm, "end": v(-21.26, 11.14) * mm});
            skLineSegment(sketch, "E335", {"start": v(-21.26, 11.14) * mm, "end": v(-21.26, -1.13) * mm});
            skLineSegment(sketch, "E336", {"start": v(-21.26, -1.13) * mm, "end": v(-22.07, -1.13) * mm});
            skLineSegment(sketch, "E337", {"start": v(-22.07, -1.13) * mm, "end": v(-22.07, -1.28) * mm});
            skLineSegment(sketch, "E338", {"start": v(-22.07, -1.28) * mm, "end": v(-17.57, -1.28) * mm});
            skLineSegment(sketch, "E339", {"start": v(-17.57, -1.28) * mm, "end": v(-17.57, -1.13) * mm});
            skLineSegment(sketch, "E340", {"start": v(-17.57, -1.13) * mm, "end": v(-18.39, -1.13) * mm});
            skLineSegment(sketch, "E341", {"start": v(-18.39, -1.13) * mm, "end": v(-18.39, 11.3) * mm});
            skLineSegment(sketch, "E342", {"start": v(-13.55, 11.3) * mm, "end": v(-17.23, 11.3) * mm});
            skLineSegment(sketch, "E343", {"start": v(-17.23, 11.3) * mm, "end": v(-17.23, 11.14) * mm});
            skLineSegment(sketch, "E344", {"start": v(-17.23, 11.14) * mm, "end": v(-16.42, 11.14) * mm});
            skLineSegment(sketch, "E345", {"start": v(-16.42, 11.14) * mm, "end": v(-16.42, -1.13) * mm});
            skLineSegment(sketch, "E346", {"start": v(-16.42, -1.13) * mm, "end": v(-17.23, -1.13) * mm});
            skLineSegment(sketch, "E347", {"start": v(-17.23, -1.13) * mm, "end": v(-17.23, -1.28) * mm});
            skLineSegment(sketch, "E348", {"start": v(-17.23, -1.28) * mm, "end": v(-12.74, -1.28) * mm});
            skLineSegment(sketch, "E349", {"start": v(-12.74, -1.28) * mm, "end": v(-12.74, -1.13) * mm});
            skLineSegment(sketch, "E350", {"start": v(-12.74, -1.13) * mm, "end": v(-13.55, -1.13) * mm});
            skLineSegment(sketch, "E351", {"start": v(-13.55, -1.13) * mm, "end": v(-13.55, 11.3) * mm});
            skLineSegment(sketch, "E352", {"start": v(-3.46, 7.07) * mm, "end": v(-3.45, 7.07) * mm});
            skLineSegment(sketch, "E353", {"start": v(-3.45, 7.07) * mm, "end": v(-3.33, 7.07) * mm});
            skLineSegment(sketch, "E354", {"start": v(-3.33, 7.07) * mm, "end": v(-2.99, 6.8) * mm});
            skLineSegment(sketch, "E355", {"start": v(-2.99, 6.8) * mm, "end": v(-2.67, 6.05) * mm});
            skLineSegment(sketch, "E356", {"start": v(-2.67, 6.05) * mm, "end": v(-2.48, 4.79) * mm});
            skLineSegment(sketch, "E357", {"start": v(-2.48, 4.79) * mm, "end": v(-2.41, 3.43) * mm});
            skLineSegment(sketch, "E358", {"start": v(-2.41, 3.43) * mm, "end": v(-2.4, 2.97) * mm});
            skLineSegment(sketch, "E359", {"start": v(-2.4, 2.97) * mm, "end": v(-4.48, 2.97) * mm});
            skLineSegment(sketch, "E360", {"start": v(-4.48, 2.97) * mm, "end": v(-4.48, 3.32) * mm});
            skLineSegment(sketch, "E361", {"start": v(-4.48, 3.32) * mm, "end": v(-4.44, 4.34) * mm});
            skLineSegment(sketch, "E362", {"start": v(-4.44, 4.34) * mm, "end": v(-4.3, 5.65) * mm});
            skLineSegment(sketch, "E363", {"start": v(-4.3, 5.65) * mm, "end": v(-4, 6.65) * mm});
            skLineSegment(sketch, "E364", {"start": v(-4, 6.65) * mm, "end": v(-3.6, 7.06) * mm});
            skLineSegment(sketch, "E365", {"start": v(-3.6, 7.06) * mm, "end": v(-3.46, 7.07) * mm});
            skLineSegment(sketch, "E366", {"start": v(0.43, 2.79) * mm, "end": v(0.43, 2.95) * mm});
            skLineSegment(sketch, "E367", {"start": v(0.43, 2.95) * mm, "end": v(0.42, 3.24) * mm});
            skLineSegment(sketch, "E368", {"start": v(0.42, 3.24) * mm, "end": v(0.11, 4.6) * mm});
            skLineSegment(sketch, "E369", {"start": v(0.11, 4.6) * mm, "end": v(-0.54, 5.79) * mm});
            skLineSegment(sketch, "E370", {"start": v(-0.54, 5.79) * mm, "end": v(-0.72, 5.99) * mm});
            skLineSegment(sketch, "E371", {"start": v(-0.72, 5.99) * mm, "end": v(-0.9, 6.19) * mm});
            skLineSegment(sketch, "E372", {"start": v(-0.9, 6.19) * mm, "end": v(-1.96, 6.9) * mm});
            skLineSegment(sketch, "E373", {"start": v(-1.96, 6.9) * mm, "end": v(-3.07, 7.22) * mm});
            skLineSegment(sketch, "E374", {"start": v(-3.07, 7.22) * mm, "end": v(-3.44, 7.22) * mm});
            skLineSegment(sketch, "E375", {"start": v(-3.44, 7.22) * mm, "end": v(-3.81, 7.22) * mm});
            skLineSegment(sketch, "E376", {"start": v(-3.81, 7.22) * mm, "end": v(-4.93, 6.9) * mm});
            skLineSegment(sketch, "E377", {"start": v(-4.93, 6.9) * mm, "end": v(-6.14, 6) * mm});
            skLineSegment(sketch, "E378", {"start": v(-6.14, 6) * mm, "end": v(-6.97, 4.64) * mm});
            skLineSegment(sketch, "E379", {"start": v(-6.97, 4.64) * mm, "end": v(-7.3, 3.4) * mm});
            skLineSegment(sketch, "E380", {"start": v(-7.3, 3.4) * mm, "end": v(-7.3, 2.97) * mm});
            skLineSegment(sketch, "E381", {"start": v(-7.3, 2.97) * mm, "end": v(-8.72, 2.97) * mm});
            skLineSegment(sketch, "E382", {"start": v(-8.72, 2.97) * mm, "end": v(-8.72, 7.03) * mm});
            skLineSegment(sketch, "E383", {"start": v(-8.72, 7.03) * mm, "end": v(-12.4, 7.03) * mm});
            skLineSegment(sketch, "E384", {"start": v(-12.4, 7.03) * mm, "end": v(-12.4, 6.88) * mm});
            skLineSegment(sketch, "E385", {"start": v(-12.4, 6.88) * mm, "end": v(-11.59, 6.88) * mm});
            skLineSegment(sketch, "E386", {"start": v(-11.59, 6.88) * mm, "end": v(-11.59, -1.13) * mm});
            skLineSegment(sketch, "E387", {"start": v(-11.59, -1.13) * mm, "end": v(-12.4, -1.13) * mm});
            skLineSegment(sketch, "E388", {"start": v(-12.4, -1.13) * mm, "end": v(-12.4, -1.28) * mm});
            skLineSegment(sketch, "E389", {"start": v(-12.4, -1.28) * mm, "end": v(-7.9, -1.28) * mm});
            skLineSegment(sketch, "E390", {"start": v(-7.9, -1.28) * mm, "end": v(-7.9, -1.13) * mm});
            skLineSegment(sketch, "E391", {"start": v(-7.9, -1.13) * mm, "end": v(-8.72, -1.13) * mm});
            skLineSegment(sketch, "E392", {"start": v(-8.72, -1.13) * mm, "end": v(-8.72, 2.79) * mm});
            skLineSegment(sketch, "E393", {"start": v(-8.72, 2.79) * mm, "end": v(-7.3, 2.79) * mm});
            skLineSegment(sketch, "E394", {"start": v(-7.3, 2.79) * mm, "end": v(-7.3, 2.38) * mm});
            skLineSegment(sketch, "E395", {"start": v(-7.3, 2.38) * mm, "end": v(-7, 1.17) * mm});
            skLineSegment(sketch, "E396", {"start": v(-7, 1.17) * mm, "end": v(-6.2, -0.16) * mm});
            skLineSegment(sketch, "E397", {"start": v(-6.2, -0.16) * mm, "end": v(-5.02, -1.07) * mm});
            skLineSegment(sketch, "E398", {"start": v(-5.02, -1.07) * mm, "end": v(-3.93, -1.42) * mm});
            skLineSegment(sketch, "E399", {"start": v(-3.93, -1.42) * mm, "end": v(-3.57, -1.43) * mm});
            skLineSegment(sketch, "E400", {"start": v(-3.57, -1.43) * mm, "end": v(-3.49, -1.43) * mm});
            skLineSegment(sketch, "E401", {"start": v(-3.49, -1.43) * mm, "end": v(-3.24, -1.42) * mm});
            skLineSegment(sketch, "E402", {"start": v(-3.24, -1.42) * mm, "end": v(-2.8, -1.36) * mm});
            skLineSegment(sketch, "E403", {"start": v(-2.8, -1.36) * mm, "end": v(-2.28, -1.22) * mm});
            skLineSegment(sketch, "E404", {"start": v(-2.28, -1.22) * mm, "end": v(-1.72, -1) * mm});
            skLineSegment(sketch, "E405", {"start": v(-1.72, -1) * mm, "end": v(-1.15, -0.63) * mm});
            skLineSegment(sketch, "E406", {"start": v(-1.15, -0.63) * mm, "end": v(-0.61, -0.13) * mm});
            skLineSegment(sketch, "E407", {"start": v(-0.61, -0.13) * mm, "end": v(-0.14, 0.56) * mm});
            skLineSegment(sketch, "E408", {"start": v(-0.14, 0.56) * mm, "end": v(0.16, 1.22) * mm});
            skLineSegment(sketch, "E409", {"start": v(0.16, 1.22) * mm, "end": v(0.24, 1.45) * mm});
            skLineSegment(sketch, "E410", {"start": v(0.24, 1.45) * mm, "end": v(0.25, 1.52) * mm});
            skLineSegment(sketch, "E411", {"start": v(0.25, 1.52) * mm, "end": v(0.1, 1.52) * mm});
            skLineSegment(sketch, "E412", {"start": v(0.1, 1.52) * mm, "end": v(-0.02, 1.2) * mm});
            skLineSegment(sketch, "E413", {"start": v(-0.02, 1.2) * mm, "end": v(-0.1, 0.97) * mm});
            skLineSegment(sketch, "E414", {"start": v(-0.1, 0.97) * mm, "end": v(-0.74, 0) * mm});
            skLineSegment(sketch, "E415", {"start": v(-0.74, 0) * mm, "end": v(-1.6, -0.74) * mm});
            skLineSegment(sketch, "E416", {"start": v(-1.6, -0.74) * mm, "end": v(-1.8, -0.85) * mm});
            skLineSegment(sketch, "E417", {"start": v(-1.8, -0.85) * mm, "end": v(-1.9, -0.9) * mm});
            skLineSegment(sketch, "E418", {"start": v(-1.9, -0.9) * mm, "end": v(-2.64, -1.13) * mm});
            skLineSegment(sketch, "E419", {"start": v(-2.64, -1.13) * mm, "end": v(-2.88, -1.13) * mm});
            skLineSegment(sketch, "E420", {"start": v(-2.88, -1.13) * mm, "end": v(-3.1, -1.13) * mm});
            skLineSegment(sketch, "E421", {"start": v(-3.1, -1.13) * mm, "end": v(-3.69, -0.84) * mm});
            skLineSegment(sketch, "E422", {"start": v(-3.69, -0.84) * mm, "end": v(-3.74, -0.78) * mm});
            skLineSegment(sketch, "E423", {"start": v(-3.74, -0.78) * mm, "end": v(-3.89, -0.64) * mm});
            skLineSegment(sketch, "E424", {"start": v(-3.89, -0.64) * mm, "end": v(-4.17, -0.06) * mm});
            skLineSegment(sketch, "E425", {"start": v(-4.17, -0.06) * mm, "end": v(-4.39, 0.88) * mm});
            skLineSegment(sketch, "E426", {"start": v(-4.39, 0.88) * mm, "end": v(-4.47, 1.88) * mm});
            skLineSegment(sketch, "E427", {"start": v(-4.47, 1.88) * mm, "end": v(-4.48, 2.56) * mm});
            skLineSegment(sketch, "E428", {"start": v(-4.48, 2.56) * mm, "end": v(-4.48, 2.79) * mm});
            skLineSegment(sketch, "E429", {"start": v(-4.48, 2.79) * mm, "end": v(0.43, 2.79) * mm});
            skLineSegment(sketch, "E430", {"start": v(-37.5, -9.57) * mm, "end": v(-37.5, -9.75) * mm});
            skLineSegment(sketch, "E431", {"start": v(-37.5, -9.75) * mm, "end": v(-19.8, -9.75) * mm});
            skLineSegment(sketch, "E432", {"start": v(-19.8, -9.75) * mm, "end": v(-19.8, -9.57) * mm});
            skLineSegment(sketch, "E433", {"start": v(-19.8, -9.57) * mm, "end": v(-37.5, -9.57) * mm});
            skLineSegment(sketch, "E434", {"start": v(19.8, -9.57) * mm, "end": v(19.8, -9.75) * mm});
            skLineSegment(sketch, "E435", {"start": v(19.8, -9.75) * mm, "end": v(37.5, -9.75) * mm});
            skLineSegment(sketch, "E436", {"start": v(37.5, -9.75) * mm, "end": v(37.5, -9.57) * mm});
            skLineSegment(sketch, "E437", {"start": v(37.5, -9.57) * mm, "end": v(19.8, -9.57) * mm});
            skLineSegment(sketch, "E438", {"start": v(15.03, 7.07) * mm, "end": v(15.05, 7.07) * mm});
            skLineSegment(sketch, "E439", {"start": v(15.05, 7.07) * mm, "end": v(15.17, 7.07) * mm});
            skLineSegment(sketch, "E440", {"start": v(15.17, 7.07) * mm, "end": v(15.5, 6.8) * mm});
            skLineSegment(sketch, "E441", {"start": v(15.5, 6.8) * mm, "end": v(15.83, 6.05) * mm});
            skLineSegment(sketch, "E442", {"start": v(15.83, 6.05) * mm, "end": v(16.02, 4.79) * mm});
            skLineSegment(sketch, "E443", {"start": v(16.02, 4.79) * mm, "end": v(16.08, 3.43) * mm});
            skLineSegment(sketch, "E444", {"start": v(16.08, 3.43) * mm, "end": v(16.08, 2.97) * mm});
            skLineSegment(sketch, "E445", {"start": v(16.08, 2.97) * mm, "end": v(14.02, 2.97) * mm});
            skLineSegment(sketch, "E446", {"start": v(14.02, 2.97) * mm, "end": v(14.02, 3.32) * mm});
            skLineSegment(sketch, "E447", {"start": v(14.02, 3.32) * mm, "end": v(14.05, 4.34) * mm});
            skLineSegment(sketch, "E448", {"start": v(14.05, 4.34) * mm, "end": v(14.2, 5.65) * mm});
            skLineSegment(sketch, "E449", {"start": v(14.2, 5.65) * mm, "end": v(14.5, 6.65) * mm});
            skLineSegment(sketch, "E450", {"start": v(14.5, 6.65) * mm, "end": v(14.9, 7.06) * mm});
            skLineSegment(sketch, "E451", {"start": v(14.9, 7.06) * mm, "end": v(15.03, 7.07) * mm});
            skLineSegment(sketch, "E452", {"start": v(18.92, 2.79) * mm, "end": v(18.92, 2.95) * mm});
            skLineSegment(sketch, "E453", {"start": v(18.92, 2.95) * mm, "end": v(18.91, 3.24) * mm});
            skLineSegment(sketch, "E454", {"start": v(18.91, 3.24) * mm, "end": v(18.6, 4.6) * mm});
            skLineSegment(sketch, "E455", {"start": v(18.6, 4.6) * mm, "end": v(17.95, 5.79) * mm});
            skLineSegment(sketch, "E456", {"start": v(17.95, 5.79) * mm, "end": v(17.77, 5.99) * mm});
            skLineSegment(sketch, "E457", {"start": v(17.77, 5.99) * mm, "end": v(17.6, 6.19) * mm});
            skLineSegment(sketch, "E458", {"start": v(17.6, 6.19) * mm, "end": v(16.53, 6.9) * mm});
            skLineSegment(sketch, "E459", {"start": v(16.53, 6.9) * mm, "end": v(15.42, 7.22) * mm});
            skLineSegment(sketch, "E460", {"start": v(15.42, 7.22) * mm, "end": v(15.06, 7.22) * mm});
            skLineSegment(sketch, "E461", {"start": v(15.06, 7.22) * mm, "end": v(14.69, 7.22) * mm});
            skLineSegment(sketch, "E462", {"start": v(14.69, 7.22) * mm, "end": v(13.58, 6.9) * mm});
            skLineSegment(sketch, "E463", {"start": v(13.58, 6.9) * mm, "end": v(12.52, 6.19) * mm});
            skLineSegment(sketch, "E464", {"start": v(12.52, 6.19) * mm, "end": v(12.34, 5.99) * mm});
            skLineSegment(sketch, "E465", {"start": v(12.34, 5.99) * mm, "end": v(12.16, 5.8) * mm});
            skLineSegment(sketch, "E466", {"start": v(12.16, 5.8) * mm, "end": v(11.5, 4.62) * mm});
            skLineSegment(sketch, "E467", {"start": v(11.5, 4.62) * mm, "end": v(11.2, 3.26) * mm});
            skLineSegment(sketch, "E468", {"start": v(11.2, 3.26) * mm, "end": v(11.2, 2.97) * mm});
            skLineSegment(sketch, "E469", {"start": v(11.2, 2.97) * mm, "end": v(9.75, 2.97) * mm});
            skLineSegment(sketch, "E470", {"start": v(9.75, 2.97) * mm, "end": v(9.75, 11.14) * mm});
            skLineSegment(sketch, "E471", {"start": v(9.75, 11.14) * mm, "end": v(11.4, 11.14) * mm});
            skLineSegment(sketch, "E472", {"start": v(11.4, 11.14) * mm, "end": v(11.4, 11.3) * mm});
            skLineSegment(sketch, "E473", {"start": v(11.4, 11.3) * mm, "end": v(4.9, 11.3) * mm});
            skLineSegment(sketch, "E474", {"start": v(4.9, 11.3) * mm, "end": v(4.9, 11.14) * mm});
            skLineSegment(sketch, "E475", {"start": v(4.9, 11.14) * mm, "end": v(6.54, 11.14) * mm});
            skLineSegment(sketch, "E476", {"start": v(6.54, 11.14) * mm, "end": v(6.54, 0.95) * mm});
            skLineSegment(sketch, "E477", {"start": v(6.54, 0.95) * mm, "end": v(6.54, 0.73) * mm});
            skLineSegment(sketch, "E478", {"start": v(6.54, 0.73) * mm, "end": v(6.4, 0.08) * mm});
            skLineSegment(sketch, "E479", {"start": v(6.4, 0.08) * mm, "end": v(6.01, -0.52) * mm});
            skLineSegment(sketch, "E480", {"start": v(6.01, -0.52) * mm, "end": v(5.48, -0.88) * mm});
            skLineSegment(sketch, "E481", {"start": v(5.48, -0.88) * mm, "end": v(5.04, -1) * mm});
            skLineSegment(sketch, "E482", {"start": v(5.04, -1) * mm, "end": v(4.89, -1) * mm});
            skLineSegment(sketch, "E483", {"start": v(4.89, -1) * mm, "end": v(4.66, -1) * mm});
            skLineSegment(sketch, "E484", {"start": v(4.66, -1) * mm, "end": v(3.96, -0.72) * mm});
            skLineSegment(sketch, "E485", {"start": v(3.96, -0.72) * mm, "end": v(3.34, -0.13) * mm});
            skLineSegment(sketch, "E486", {"start": v(3.34, -0.13) * mm, "end": v(3.25, 0.03) * mm});
            skLineSegment(sketch, "E487", {"start": v(3.25, 0.03) * mm, "end": v(3.32, -0.03) * mm});
            skLineSegment(sketch, "E488", {"start": v(3.32, -0.03) * mm, "end": v(3.99, -0.32) * mm});
            skLineSegment(sketch, "E489", {"start": v(3.99, -0.32) * mm, "end": v(4.21, -0.32) * mm});
            skLineSegment(sketch, "E490", {"start": v(4.21, -0.32) * mm, "end": v(4.35, -0.32) * mm});
            skLineSegment(sketch, "E491", {"start": v(4.35, -0.32) * mm, "end": v(4.77, -0.2) * mm});
            skLineSegment(sketch, "E492", {"start": v(4.77, -0.2) * mm, "end": v(5.23, 0.1) * mm});
            skLineSegment(sketch, "E493", {"start": v(5.23, 0.1) * mm, "end": v(5.53, 0.55) * mm});
            skLineSegment(sketch, "E494", {"start": v(5.53, 0.55) * mm, "end": v(5.65, 0.97) * mm});
            skLineSegment(sketch, "E495", {"start": v(5.65, 0.97) * mm, "end": v(5.65, 1.11) * mm});
            skLineSegment(sketch, "E496", {"start": v(5.65, 1.11) * mm, "end": v(5.65, 1.25) * mm});
            skLineSegment(sketch, "E497", {"start": v(5.65, 1.25) * mm, "end": v(5.53, 1.67) * mm});
            skLineSegment(sketch, "E498", {"start": v(5.53, 1.67) * mm, "end": v(5.23, 2.13) * mm});
            skLineSegment(sketch, "E499", {"start": v(5.23, 2.13) * mm, "end": v(4.77, 2.44) * mm});
            skLineSegment(sketch, "E500", {"start": v(4.77, 2.44) * mm, "end": v(4.35, 2.55) * mm});
            skLineSegment(sketch, "E501", {"start": v(4.35, 2.55) * mm, "end": v(4.21, 2.55) * mm});
            skLineSegment(sketch, "E502", {"start": v(4.21, 2.55) * mm, "end": v(4.07, 2.55) * mm});
            skLineSegment(sketch, "E503", {"start": v(4.07, 2.55) * mm, "end": v(3.65, 2.44) * mm});
            skLineSegment(sketch, "E504", {"start": v(3.65, 2.44) * mm, "end": v(3.2, 2.15) * mm});
            skLineSegment(sketch, "E505", {"start": v(3.2, 2.15) * mm, "end": v(2.89, 1.71) * mm});
            skLineSegment(sketch, "E506", {"start": v(2.89, 1.71) * mm, "end": v(2.78, 1.31) * mm});
            skLineSegment(sketch, "E507", {"start": v(2.78, 1.31) * mm, "end": v(2.78, 1.18) * mm});
            skLineSegment(sketch, "E508", {"start": v(2.78, 1.18) * mm, "end": v(2.78, 0.95) * mm});
            skLineSegment(sketch, "E509", {"start": v(2.78, 0.95) * mm, "end": v(2.95, 0.25) * mm});
            skLineSegment(sketch, "E510", {"start": v(2.95, 0.25) * mm, "end": v(3.5, -0.6) * mm});
            skLineSegment(sketch, "E511", {"start": v(3.5, -0.6) * mm, "end": v(4.5, -1.22) * mm});
            skLineSegment(sketch, "E512", {"start": v(4.5, -1.22) * mm, "end": v(5.64, -1.47) * mm});
            skLineSegment(sketch, "E513", {"start": v(5.64, -1.47) * mm, "end": v(6.02, -1.47) * mm});
            skLineSegment(sketch, "E514", {"start": v(6.02, -1.47) * mm, "end": v(6.18, -1.47) * mm});
            skLineSegment(sketch, "E515", {"start": v(6.18, -1.47) * mm, "end": v(6.67, -1.44) * mm});
            skLineSegment(sketch, "E516", {"start": v(6.67, -1.44) * mm, "end": v(7.33, -1.36) * mm});
            skLineSegment(sketch, "E517", {"start": v(7.33, -1.36) * mm, "end": v(7.95, -1.2) * mm});
            skLineSegment(sketch, "E518", {"start": v(7.95, -1.2) * mm, "end": v(8.52, -0.91) * mm});
            skLineSegment(sketch, "E519", {"start": v(8.52, -0.91) * mm, "end": v(9.01, -0.5) * mm});
            skLineSegment(sketch, "E520", {"start": v(9.01, -0.5) * mm, "end": v(9.4, 0.1) * mm});
            skLineSegment(sketch, "E521", {"start": v(9.4, 0.1) * mm, "end": v(9.65, 0.86) * mm});
            skLineSegment(sketch, "E522", {"start": v(9.65, 0.86) * mm, "end": v(9.75, 1.6) * mm});
            skLineSegment(sketch, "E523", {"start": v(9.75, 1.6) * mm, "end": v(9.75, 1.85) * mm});
            skLineSegment(sketch, "E524", {"start": v(9.75, 1.85) * mm, "end": v(9.75, 2.79) * mm});
            skLineSegment(sketch, "E525", {"start": v(9.75, 2.79) * mm, "end": v(11.2, 2.79) * mm});
            skLineSegment(sketch, "E526", {"start": v(11.2, 2.79) * mm, "end": v(11.2, 2.38) * mm});
            skLineSegment(sketch, "E527", {"start": v(11.2, 2.38) * mm, "end": v(11.5, 1.17) * mm});
            skLineSegment(sketch, "E528", {"start": v(11.5, 1.17) * mm, "end": v(12.3, -0.16) * mm});
            skLineSegment(sketch, "E529", {"start": v(12.3, -0.16) * mm, "end": v(13.48, -1.07) * mm});
            skLineSegment(sketch, "E530", {"start": v(13.48, -1.07) * mm, "end": v(14.56, -1.42) * mm});
            skLineSegment(sketch, "E531", {"start": v(14.56, -1.42) * mm, "end": v(14.93, -1.43) * mm});
            skLineSegment(sketch, "E532", {"start": v(14.93, -1.43) * mm, "end": v(15.01, -1.43) * mm});
            skLineSegment(sketch, "E533", {"start": v(15.01, -1.43) * mm, "end": v(15.25, -1.42) * mm});
            skLineSegment(sketch, "E534", {"start": v(15.25, -1.42) * mm, "end": v(15.7, -1.36) * mm});
            skLineSegment(sketch, "E535", {"start": v(15.7, -1.36) * mm, "end": v(16.21, -1.22) * mm});
            skLineSegment(sketch, "E536", {"start": v(16.21, -1.22) * mm, "end": v(16.77, -1) * mm});
            skLineSegment(sketch, "E537", {"start": v(16.77, -1) * mm, "end": v(17.34, -0.63) * mm});
            skLineSegment(sketch, "E538", {"start": v(17.34, -0.63) * mm, "end": v(17.88, -0.13) * mm});
            skLineSegment(sketch, "E539", {"start": v(17.88, -0.13) * mm, "end": v(18.35, 0.56) * mm});
            skLineSegment(sketch, "E540", {"start": v(18.35, 0.56) * mm, "end": v(18.66, 1.22) * mm});
            skLineSegment(sketch, "E541", {"start": v(18.66, 1.22) * mm, "end": v(18.73, 1.45) * mm});
            skLineSegment(sketch, "E542", {"start": v(18.73, 1.45) * mm, "end": v(18.75, 1.52) * mm});
            skLineSegment(sketch, "E543", {"start": v(18.75, 1.52) * mm, "end": v(18.6, 1.52) * mm});
            skLineSegment(sketch, "E544", {"start": v(18.6, 1.52) * mm, "end": v(18.48, 1.2) * mm});
            skLineSegment(sketch, "E545", {"start": v(18.48, 1.2) * mm, "end": v(18.4, 0.97) * mm});
            skLineSegment(sketch, "E546", {"start": v(18.4, 0.97) * mm, "end": v(17.76, 0) * mm});
            skLineSegment(sketch, "E547", {"start": v(17.76, 0) * mm, "end": v(16.9, -0.74) * mm});
            skLineSegment(sketch, "E548", {"start": v(16.9, -0.74) * mm, "end": v(16.69, -0.85) * mm});
            skLineSegment(sketch, "E549", {"start": v(16.69, -0.85) * mm, "end": v(16.59, -0.9) * mm});
            skLineSegment(sketch, "E550", {"start": v(16.59, -0.9) * mm, "end": v(15.86, -1.13) * mm});
            skLineSegment(sketch, "E551", {"start": v(15.86, -1.13) * mm, "end": v(15.61, -1.13) * mm});
            skLineSegment(sketch, "E552", {"start": v(15.61, -1.13) * mm, "end": v(15.4, -1.13) * mm});
            skLineSegment(sketch, "E553", {"start": v(15.4, -1.13) * mm, "end": v(14.8, -0.84) * mm});
            skLineSegment(sketch, "E554", {"start": v(14.8, -0.84) * mm, "end": v(14.75, -0.78) * mm});
            skLineSegment(sketch, "E555", {"start": v(14.75, -0.78) * mm, "end": v(14.6, -0.64) * mm});
            skLineSegment(sketch, "E556", {"start": v(14.6, -0.64) * mm, "end": v(14.33, -0.06) * mm});
            skLineSegment(sketch, "E557", {"start": v(14.33, -0.06) * mm, "end": v(14.1, 0.88) * mm});
            skLineSegment(sketch, "E558", {"start": v(14.1, 0.88) * mm, "end": v(14.03, 1.88) * mm});
            skLineSegment(sketch, "E559", {"start": v(14.03, 1.88) * mm, "end": v(14.02, 2.56) * mm});
            skLineSegment(sketch, "E560", {"start": v(14.02, 2.56) * mm, "end": v(14.02, 2.79) * mm});
            skLineSegment(sketch, "E561", {"start": v(14.02, 2.79) * mm, "end": v(18.92, 2.79) * mm});
            skLineSegment(sketch, "E562", {"start": v(23.92, 0.63) * mm, "end": v(23.92, 0.53) * mm});
            skLineSegment(sketch, "E563", {"start": v(23.92, 0.53) * mm, "end": v(23.65, -0.38) * mm});
            skLineSegment(sketch, "E564", {"start": v(23.65, -0.38) * mm, "end": v(23.6, -0.47) * mm});
            skLineSegment(sketch, "E565", {"start": v(23.6, -0.47) * mm, "end": v(23.55, -0.54) * mm});
            skLineSegment(sketch, "E566", {"start": v(23.55, -0.54) * mm, "end": v(23.23, -0.85) * mm});
            skLineSegment(sketch, "E567", {"start": v(23.23, -0.85) * mm, "end": v(23.12, -0.85) * mm});
            skLineSegment(sketch, "E568", {"start": v(23.12, -0.85) * mm, "end": v(23.09, -0.85) * mm});
            skLineSegment(sketch, "E569", {"start": v(23.09, -0.85) * mm, "end": v(23, -0.8) * mm});
            skLineSegment(sketch, "E570", {"start": v(23, -0.8) * mm, "end": v(22.87, -0.56) * mm});
            skLineSegment(sketch, "E571", {"start": v(22.87, -0.56) * mm, "end": v(22.76, -0.04) * mm});
            skLineSegment(sketch, "E572", {"start": v(22.76, -0.04) * mm, "end": v(22.72, 0.62) * mm});
            skLineSegment(sketch, "E573", {"start": v(22.72, 0.62) * mm, "end": v(22.72, 0.84) * mm});
            skLineSegment(sketch, "E574", {"start": v(22.72, 0.84) * mm, "end": v(22.72, 1.12) * mm});
            skLineSegment(sketch, "E575", {"start": v(22.72, 1.12) * mm, "end": v(22.77, 1.93) * mm});
            skLineSegment(sketch, "E576", {"start": v(22.77, 1.93) * mm, "end": v(22.88, 2.61) * mm});
            skLineSegment(sketch, "E577", {"start": v(22.88, 2.61) * mm, "end": v(23.05, 3) * mm});
            skLineSegment(sketch, "E578", {"start": v(23.05, 3) * mm, "end": v(23.19, 3.15) * mm});
            skLineSegment(sketch, "E579", {"start": v(23.19, 3.15) * mm, "end": v(23.25, 3.18) * mm});
            skLineSegment(sketch, "E580", {"start": v(23.25, 3.18) * mm, "end": v(23.31, 3.23) * mm});
            skLineSegment(sketch, "E581", {"start": v(23.31, 3.23) * mm, "end": v(23.88, 3.79) * mm});
            skLineSegment(sketch, "E582", {"start": v(23.88, 3.79) * mm, "end": v(23.92, 3.87) * mm});
            skLineSegment(sketch, "E583", {"start": v(23.92, 3.87) * mm, "end": v(23.92, 0.63) * mm});
            skLineSegment(sketch, "E584", {"start": v(28.3, 0.14) * mm, "end": v(28.3, -0.01) * mm});
            skLineSegment(sketch, "E585", {"start": v(28.3, -0.01) * mm, "end": v(28.09, -0.47) * mm});
            skLineSegment(sketch, "E586", {"start": v(28.09, -0.47) * mm, "end": v(27.68, -0.7) * mm});
            skLineSegment(sketch, "E587", {"start": v(27.68, -0.7) * mm, "end": v(27.54, -0.7) * mm});
            skLineSegment(sketch, "E588", {"start": v(27.54, -0.7) * mm, "end": v(27.4, -0.7) * mm});
            skLineSegment(sketch, "E589", {"start": v(27.4, -0.7) * mm, "end": v(27.02, -0.48) * mm});
            skLineSegment(sketch, "E590", {"start": v(27.02, -0.48) * mm, "end": v(26.8, -0.06) * mm});
            skLineSegment(sketch, "E591", {"start": v(26.8, -0.06) * mm, "end": v(26.8, 0.04) * mm});
            skLineSegment(sketch, "E592", {"start": v(26.8, 0.04) * mm, "end": v(26.8, 3.9) * mm});
            skLineSegment(sketch, "E593", {"start": v(26.8, 3.9) * mm, "end": v(26.8, 4.32) * mm});
            skLineSegment(sketch, "E594", {"start": v(26.8, 4.32) * mm, "end": v(26.48, 5.58) * mm});
            skLineSegment(sketch, "E595", {"start": v(26.48, 5.58) * mm, "end": v(25.68, 6.6) * mm});
            skLineSegment(sketch, "E596", {"start": v(25.68, 6.6) * mm, "end": v(24.58, 7.1) * mm});
            skLineSegment(sketch, "E597", {"start": v(24.58, 7.1) * mm, "end": v(23.7, 7.22) * mm});
            skLineSegment(sketch, "E598", {"start": v(23.7, 7.22) * mm, "end": v(23.4, 7.22) * mm});
            skLineSegment(sketch, "E599", {"start": v(23.4, 7.22) * mm, "end": v(23.04, 7.22) * mm});
            skLineSegment(sketch, "E600", {"start": v(23.04, 7.22) * mm, "end": v(21.95, 7) * mm});
            skLineSegment(sketch, "E601", {"start": v(21.95, 7) * mm, "end": v(21.02, 6.49) * mm});
            skLineSegment(sketch, "E602", {"start": v(21.02, 6.49) * mm, "end": v(20.88, 6.34) * mm});
            skLineSegment(sketch, "E603", {"start": v(20.88, 6.34) * mm, "end": v(20.76, 6.23) * mm});
            skLineSegment(sketch, "E604", {"start": v(20.76, 6.23) * mm, "end": v(20.34, 5.54) * mm});
            skLineSegment(sketch, "E605", {"start": v(20.34, 5.54) * mm, "end": v(20.16, 4.74) * mm});
            skLineSegment(sketch, "E606", {"start": v(20.16, 4.74) * mm, "end": v(20.16, 4.57) * mm});
            skLineSegment(sketch, "E607", {"start": v(20.16, 4.57) * mm, "end": v(20.17, 4.44) * mm});
            skLineSegment(sketch, "E608", {"start": v(20.17, 4.44) * mm, "end": v(20.3, 4.04) * mm});
            skLineSegment(sketch, "E609", {"start": v(20.3, 4.04) * mm, "end": v(20.6, 3.6) * mm});
            skLineSegment(sketch, "E610", {"start": v(20.6, 3.6) * mm, "end": v(21.05, 3.31) * mm});
            skLineSegment(sketch, "E611", {"start": v(21.05, 3.31) * mm, "end": v(21.46, 3.2) * mm});
            skLineSegment(sketch, "E612", {"start": v(21.46, 3.2) * mm, "end": v(21.6, 3.2) * mm});
            skLineSegment(sketch, "E613", {"start": v(21.6, 3.2) * mm, "end": v(21.73, 3.2) * mm});
            skLineSegment(sketch, "E614", {"start": v(21.73, 3.2) * mm, "end": v(22.15, 3.32) * mm});
            skLineSegment(sketch, "E615", {"start": v(22.15, 3.32) * mm, "end": v(22.6, 3.63) * mm});
            skLineSegment(sketch, "E616", {"start": v(22.6, 3.63) * mm, "end": v(22.92, 4.08) * mm});
            skLineSegment(sketch, "E617", {"start": v(22.92, 4.08) * mm, "end": v(23.03, 4.5) * mm});
            skLineSegment(sketch, "E618", {"start": v(23.03, 4.5) * mm, "end": v(23.03, 4.64) * mm});
            skLineSegment(sketch, "E619", {"start": v(23.03, 4.64) * mm, "end": v(23.03, 4.78) * mm});
            skLineSegment(sketch, "E620", {"start": v(23.03, 4.78) * mm, "end": v(22.92, 5.2) * mm});
            skLineSegment(sketch, "E621", {"start": v(22.92, 5.2) * mm, "end": v(22.6, 5.66) * mm});
            skLineSegment(sketch, "E622", {"start": v(22.6, 5.66) * mm, "end": v(22.15, 5.96) * mm});
            skLineSegment(sketch, "E623", {"start": v(22.15, 5.96) * mm, "end": v(21.73, 6.08) * mm});
            skLineSegment(sketch, "E624", {"start": v(21.73, 6.08) * mm, "end": v(21.6, 6.08) * mm});
            skLineSegment(sketch, "E625", {"start": v(21.6, 6.08) * mm, "end": v(21.35, 6.08) * mm});
            skLineSegment(sketch, "E626", {"start": v(21.35, 6.08) * mm, "end": v(20.67, 5.77) * mm});
            skLineSegment(sketch, "E627", {"start": v(20.67, 5.77) * mm, "end": v(20.6, 5.7) * mm});
            skLineSegment(sketch, "E628", {"start": v(20.6, 5.7) * mm, "end": v(20.65, 5.81) * mm});
            skLineSegment(sketch, "E629", {"start": v(20.65, 5.81) * mm, "end": v(21.04, 6.28) * mm});
            skLineSegment(sketch, "E630", {"start": v(21.04, 6.28) * mm, "end": v(21.58, 6.67) * mm});
            skLineSegment(sketch, "E631", {"start": v(21.58, 6.67) * mm, "end": v(21.7, 6.73) * mm});
            skLineSegment(sketch, "E632", {"start": v(21.7, 6.73) * mm, "end": v(21.78, 6.77) * mm});
            skLineSegment(sketch, "E633", {"start": v(21.78, 6.77) * mm, "end": v(22.33, 6.93) * mm});
            skLineSegment(sketch, "E634", {"start": v(22.33, 6.93) * mm, "end": v(22.52, 6.93) * mm});
            skLineSegment(sketch, "E635", {"start": v(22.52, 6.93) * mm, "end": v(22.71, 6.93) * mm});
            skLineSegment(sketch, "E636", {"start": v(22.71, 6.93) * mm, "end": v(23.31, 6.6) * mm});
            skLineSegment(sketch, "E637", {"start": v(23.31, 6.6) * mm, "end": v(23.73, 5.83) * mm});
            skLineSegment(sketch, "E638", {"start": v(23.73, 5.83) * mm, "end": v(23.9, 5.02) * mm});
            skLineSegment(sketch, "E639", {"start": v(23.9, 5.02) * mm, "end": v(23.92, 4.66) * mm});
            skLineSegment(sketch, "E640", {"start": v(23.92, 4.66) * mm, "end": v(23.92, 4.54) * mm});
            skLineSegment(sketch, "E641", {"start": v(23.92, 4.54) * mm, "end": v(23.92, 4.4) * mm});
            skLineSegment(sketch, "E642", {"start": v(23.92, 4.4) * mm, "end": v(23.79, 3.96) * mm});
            skLineSegment(sketch, "E643", {"start": v(23.79, 3.96) * mm, "end": v(23.4, 3.5) * mm});
            skLineSegment(sketch, "E644", {"start": v(23.4, 3.5) * mm, "end": v(22.77, 3.17) * mm});
            skLineSegment(sketch, "E645", {"start": v(22.77, 3.17) * mm, "end": v(22.14, 3.02) * mm});
            skLineSegment(sketch, "E646", {"start": v(22.14, 3.02) * mm, "end": v(21.93, 3) * mm});
            skLineSegment(sketch, "E647", {"start": v(21.93, 3) * mm, "end": v(21.7, 2.97) * mm});
            skLineSegment(sketch, "E648", {"start": v(21.7, 2.97) * mm, "end": v(21.04, 2.77) * mm});
            skLineSegment(sketch, "E649", {"start": v(21.04, 2.77) * mm, "end": v(20.39, 2.3) * mm});
            skLineSegment(sketch, "E650", {"start": v(20.39, 2.3) * mm, "end": v(19.98, 1.62) * mm});
            skLineSegment(sketch, "E651", {"start": v(19.98, 1.62) * mm, "end": v(19.85, 0.96) * mm});
            skLineSegment(sketch, "E652", {"start": v(19.85, 0.96) * mm, "end": v(19.85, 0.74) * mm});
            skLineSegment(sketch, "E653", {"start": v(19.85, 0.74) * mm, "end": v(19.85, 0.52) * mm});
            skLineSegment(sketch, "E654", {"start": v(19.85, 0.52) * mm, "end": v(20, -0.15) * mm});
            skLineSegment(sketch, "E655", {"start": v(20, -0.15) * mm, "end": v(20.42, -0.84) * mm});
            skLineSegment(sketch, "E656", {"start": v(20.42, -0.84) * mm, "end": v(21.07, -1.28) * mm});
            skLineSegment(sketch, "E657", {"start": v(21.07, -1.28) * mm, "end": v(21.72, -1.43) * mm});
            skLineSegment(sketch, "E658", {"start": v(21.72, -1.43) * mm, "end": v(21.94, -1.43) * mm});
            skLineSegment(sketch, "E659", {"start": v(21.94, -1.43) * mm, "end": v(22.16, -1.43) * mm});
            skLineSegment(sketch, "E660", {"start": v(22.16, -1.43) * mm, "end": v(22.81, -1.28) * mm});
            skLineSegment(sketch, "E661", {"start": v(22.81, -1.28) * mm, "end": v(23.4, -0.9) * mm});
            skLineSegment(sketch, "E662", {"start": v(23.4, -0.9) * mm, "end": v(23.77, -0.47) * mm});
            skLineSegment(sketch, "E663", {"start": v(23.77, -0.47) * mm, "end": v(23.92, -0.19) * mm});
            skLineSegment(sketch, "E664", {"start": v(23.92, -0.19) * mm, "end": v(23.95, -0.1) * mm});
            skLineSegment(sketch, "E665", {"start": v(23.95, -0.1) * mm, "end": v(23.98, -0.28) * mm});
            skLineSegment(sketch, "E666", {"start": v(23.98, -0.28) * mm, "end": v(24.23, -0.82) * mm});
            skLineSegment(sketch, "E667", {"start": v(24.23, -0.82) * mm, "end": v(24.78, -1.22) * mm});
            skLineSegment(sketch, "E668", {"start": v(24.78, -1.22) * mm, "end": v(25.5, -1.4) * mm});
            skLineSegment(sketch, "E669", {"start": v(25.5, -1.4) * mm, "end": v(26.13, -1.43) * mm});
            skLineSegment(sketch, "E670", {"start": v(26.13, -1.43) * mm, "end": v(26.35, -1.43) * mm});
            skLineSegment(sketch, "E671", {"start": v(26.35, -1.43) * mm, "end": v(26.57, -1.43) * mm});
            skLineSegment(sketch, "E672", {"start": v(26.57, -1.43) * mm, "end": v(27.26, -1.33) * mm});
            skLineSegment(sketch, "E673", {"start": v(27.26, -1.33) * mm, "end": v(27.92, -1.04) * mm});
            skLineSegment(sketch, "E674", {"start": v(27.92, -1.04) * mm, "end": v(28.31, -0.55) * mm});
            skLineSegment(sketch, "E675", {"start": v(28.31, -0.55) * mm, "end": v(28.44, -0.03) * mm});
            skLineSegment(sketch, "E676", {"start": v(28.44, -0.03) * mm, "end": v(28.44, 0.14) * mm});
            skLineSegment(sketch, "E677", {"start": v(28.44, 0.14) * mm, "end": v(28.44, 0.18) * mm});
            skLineSegment(sketch, "E678", {"start": v(28.44, 0.18) * mm, "end": v(28.3, 0.2) * mm});
            skLineSegment(sketch, "E679", {"start": v(28.3, 0.2) * mm, "end": v(28.3, 0.14) * mm});
            skLineSegment(sketch, "E680", {"start": v(36.7, -1.13) * mm, "end": v(36.7, 4.96) * mm});
            skLineSegment(sketch, "E681", {"start": v(36.7, 4.96) * mm, "end": v(36.7, 5.23) * mm});
            skLineSegment(sketch, "E682", {"start": v(36.7, 5.23) * mm, "end": v(36.49, 6.02) * mm});
            skLineSegment(sketch, "E683", {"start": v(36.49, 6.02) * mm, "end": v(35.96, 6.72) * mm});
            skLineSegment(sketch, "E684", {"start": v(35.96, 6.72) * mm, "end": v(35.23, 7.1) * mm});
            skLineSegment(sketch, "E685", {"start": v(35.23, 7.1) * mm, "end": v(34.6, 7.22) * mm});
            skLineSegment(sketch, "E686", {"start": v(34.6, 7.22) * mm, "end": v(34.4, 7.22) * mm});
            skLineSegment(sketch, "E687", {"start": v(34.4, 7.22) * mm, "end": v(34.25, 7.22) * mm});
            skLineSegment(sketch, "E688", {"start": v(34.25, 7.22) * mm, "end": v(33.81, 7.15) * mm});
            skLineSegment(sketch, "E689", {"start": v(33.81, 7.15) * mm, "end": v(33.2, 6.9) * mm});
            skLineSegment(sketch, "E690", {"start": v(33.2, 6.9) * mm, "end": v(32.67, 6.45) * mm});
            skLineSegment(sketch, "E691", {"start": v(32.67, 6.45) * mm, "end": v(32.34, 5.95) * mm});
            skLineSegment(sketch, "E692", {"start": v(32.34, 5.95) * mm, "end": v(32.27, 5.77) * mm});
            skLineSegment(sketch, "E693", {"start": v(32.27, 5.77) * mm, "end": v(32.27, 7.03) * mm});
            skLineSegment(sketch, "E694", {"start": v(32.27, 7.03) * mm, "end": v(28.6, 7.03) * mm});
            skLineSegment(sketch, "E695", {"start": v(28.6, 7.03) * mm, "end": v(28.6, 6.88) * mm});
            skLineSegment(sketch, "E696", {"start": v(28.6, 6.88) * mm, "end": v(29.4, 6.88) * mm});
            skLineSegment(sketch, "E697", {"start": v(29.4, 6.88) * mm, "end": v(29.4, -1.13) * mm});
            skLineSegment(sketch, "E698", {"start": v(29.4, -1.13) * mm, "end": v(28.6, -1.13) * mm});
            skLineSegment(sketch, "E699", {"start": v(28.6, -1.13) * mm, "end": v(28.6, -1.28) * mm});
            skLineSegment(sketch, "E700", {"start": v(28.6, -1.28) * mm, "end": v(32.86, -1.28) * mm});
            skLineSegment(sketch, "E701", {"start": v(32.86, -1.28) * mm, "end": v(32.86, -1.13) * mm});
            skLineSegment(sketch, "E702", {"start": v(32.86, -1.13) * mm, "end": v(32.27, -1.13) * mm});
            skLineSegment(sketch, "E703", {"start": v(32.27, -1.13) * mm, "end": v(32.27, 5.01) * mm});
            skLineSegment(sketch, "E704", {"start": v(32.27, 5.01) * mm, "end": v(32.27, 5.33) * mm});
            skLineSegment(sketch, "E705", {"start": v(32.27, 5.33) * mm, "end": v(32.68, 6.2) * mm});
            skLineSegment(sketch, "E706", {"start": v(32.68, 6.2) * mm, "end": v(32.76, 6.3) * mm});
            skLineSegment(sketch, "E707", {"start": v(32.76, 6.3) * mm, "end": v(32.8, 6.33) * mm});
            skLineSegment(sketch, "E708", {"start": v(32.8, 6.33) * mm, "end": v(33.11, 6.51) * mm});
            skLineSegment(sketch, "E709", {"start": v(33.11, 6.51) * mm, "end": v(33.22, 6.51) * mm});
            skLineSegment(sketch, "E710", {"start": v(33.22, 6.51) * mm, "end": v(33.27, 6.51) * mm});
            skLineSegment(sketch, "E711", {"start": v(33.27, 6.51) * mm, "end": v(33.42, 6.47) * mm});
            skLineSegment(sketch, "E712", {"start": v(33.42, 6.47) * mm, "end": v(33.62, 6.3) * mm});
            skLineSegment(sketch, "E713", {"start": v(33.62, 6.3) * mm, "end": v(33.76, 5.9) * mm});
            skLineSegment(sketch, "E714", {"start": v(33.76, 5.9) * mm, "end": v(33.82, 5.36) * mm});
            skLineSegment(sketch, "E715", {"start": v(33.82, 5.36) * mm, "end": v(33.82, 5.18) * mm});
            skLineSegment(sketch, "E716", {"start": v(33.82, 5.18) * mm, "end": v(33.82, -1.13) * mm});
            skLineSegment(sketch, "E717", {"start": v(33.82, -1.13) * mm, "end": v(33.23, -1.13) * mm});
            skLineSegment(sketch, "E718", {"start": v(33.23, -1.13) * mm, "end": v(33.23, -1.28) * mm});
            skLineSegment(sketch, "E719", {"start": v(33.23, -1.28) * mm, "end": v(37.5, -1.28) * mm});
            skLineSegment(sketch, "E720", {"start": v(37.5, -1.28) * mm, "end": v(37.5, -1.13) * mm});
            skLineSegment(sketch, "E721", {"start": v(37.5, -1.13) * mm, "end": v(36.7, -1.13) * mm});
            skSolve(sketch);
        }
        {
            var Q0;
            Q0=makeQuery(id+"F2.imprint","IMPRINT",FACE,{"disambiguationData":[TD([[makeQuery(id+"F2.imprint","IMPRINT",EDGE,{"derivedFrom":sQuery(id+"F2.wireOp",EDGE,"E261")}),1.0]])]});
            var Q1;
            Q1=makeQuery(id+"F2.imprint","IMPRINT",FACE,{"disambiguationData":[TD([[makeQuery(id+"F2.imprint","IMPRINT",EDGE,{"derivedFrom":sQuery(id+"F2.wireOp",EDGE,"E322")}),1.0]])]});
            var Q2;
            Q2=makeQuery(id+"F2.imprint","IMPRINT",FACE,{"disambiguationData":[TD([[makeQuery(id+"F2.imprint","IMPRINT",EDGE,{"derivedFrom":sQuery(id+"F2.wireOp",EDGE,"E332")}),1.0]])]});
            var Q3;
            Q3=makeQuery(id+"F2.imprint","IMPRINT",FACE,{"disambiguationData":[TD([[makeQuery(id+"F2.imprint","IMPRINT",EDGE,{"derivedFrom":sQuery(id+"F2.wireOp",EDGE,"E342")}),1.0]])]});
            var Q4;
            Q4=makeQuery(id+"F2.imprint","IMPRINT",FACE,{"disambiguationData":[TD([[makeQuery(id+"F2.imprint","IMPRINT",EDGE,{"derivedFrom":sQuery(id+"F2.wireOp",EDGE,"E352")}),1.0]])]});
            var Q5;
            Q5=makeQuery(id+"F2.imprint","IMPRINT",FACE,{"disambiguationData":[TD([[makeQuery(id+"F2.imprint","IMPRINT",EDGE,{"derivedFrom":sQuery(id+"F2.wireOp",EDGE,"E237")}),1.0]])]});
            var Q6;
            Q6=makeQuery(id+"F2.imprint","IMPRINT",FACE,{"disambiguationData":[TD([[makeQuery(id+"F2.imprint","IMPRINT",EDGE,{"derivedFrom":sQuery(id+"F2.wireOp",EDGE,"E213")}),1.0]])]});
            var Q7;
            Q7=makeQuery(id+"F2.imprint","IMPRINT",FACE,{"disambiguationData":[TD([[makeQuery(id+"F2.imprint","IMPRINT",EDGE,{"derivedFrom":sQuery(id+"F2.wireOp",EDGE,"E438")}),1.0]])]});
            var Q8;
            Q8=makeQuery(id+"F2.imprint","IMPRINT",FACE,{"disambiguationData":[TD([[makeQuery(id+"F2.imprint","IMPRINT",EDGE,{"derivedFrom":sQuery(id+"F2.wireOp",EDGE,"E562")}),1.0]])]});
            var Q9;
            Q9=makeQuery(id+"F2.imprint","IMPRINT",FACE,{"disambiguationData":[TD([[makeQuery(id+"F2.imprint","IMPRINT",EDGE,{"derivedFrom":sQuery(id+"F2.wireOp",EDGE,"E680")}),1.0]])]});
            var Q10;
            Q10=makeQuery(id+"F2.imprint","IMPRINT",FACE,{"disambiguationData":[TD([[makeQuery(id+"F2.imprint","IMPRINT",EDGE,{"derivedFrom":sQuery(id+"F2.wireOp",EDGE,"E2")}),1.0]])]});
            var Q11;
            Q11=makeQuery(id+"F2.imprint","IMPRINT",FACE,{"disambiguationData":[TD([[makeQuery(id+"F2.imprint","IMPRINT",EDGE,{"derivedFrom":sQuery(id+"F2.wireOp",EDGE,"E16")}),1.0]])]});
            var Q12;
            Q12=makeQuery(id+"F2.imprint","IMPRINT",FACE,{"disambiguationData":[TD([[makeQuery(id+"F2.imprint","IMPRINT",EDGE,{"derivedFrom":sQuery(id+"F2.wireOp",EDGE,"E28")}),1.0]])]});
            var Q13;
            Q13=makeQuery(id+"F2.imprint","IMPRINT",FACE,{"disambiguationData":[TD([[makeQuery(id+"F2.imprint","IMPRINT",EDGE,{"derivedFrom":sQuery(id+"F2.wireOp",EDGE,"E34")}),1.0]])]});
            var Q14;
            Q14=makeQuery(id+"F2.imprint","IMPRINT",FACE,{"disambiguationData":[TD([[makeQuery(id+"F2.imprint","IMPRINT",EDGE,{"derivedFrom":sQuery(id+"F2.wireOp",EDGE,"E79")}),1.0]])]});
            var Q15;
            Q15=makeQuery(id+"F2.imprint","IMPRINT",FACE,{"disambiguationData":[TD([[makeQuery(id+"F2.imprint","IMPRINT",EDGE,{"derivedFrom":sQuery(id+"F2.wireOp",EDGE,"E134")}),1.0]])]});
            var Q16;
            Q16=makeQuery(id+"F2.imprint","IMPRINT",FACE,{"disambiguationData":[TD([[makeQuery(id+"F2.imprint","IMPRINT",EDGE,{"derivedFrom":sQuery(id+"F2.wireOp",EDGE,"E160")}),1.0]])]});
            var Q17;
            Q17=makeQuery(id+"F2.imprint","IMPRINT",FACE,{"disambiguationData":[TD([[makeQuery(id+"F2.imprint","IMPRINT",EDGE,{"derivedFrom":sQuery(id+"F2.wireOp",EDGE,"E189")}),1.0]])]});
            var Q18;
            Q18=makeQuery(id+"F2.imprint","IMPRINT",FACE,{"disambiguationData":[TD([[makeQuery(id+"F2.imprint","IMPRINT",EDGE,{"derivedFrom":sQuery(id+"F2.wireOp",EDGE,"E201")}),1.0]])]});
            extrude(context, id + "F3", {"entities" : qUnion([Q0, Q1, Q2, Q3, Q4, Q5, Q6, Q7, Q8, Q9, Q10, Q11, Q12, Q13, Q14, Q15, Q16, Q17, Q18]), "operationType" : NewBodyOperationType.REMOVE, "oppositeDirection" : true, "depth" : 50 * mm, "offsetDistance" : 25 * mm});
        }
        {
            var Q0;
            {var subQ0=sQuery(id+"F0.wireOp",EDGE,"E0.right");var subQ1=sQuery(id+"F0.wireOp",EDGE,"E0.bottom");var subQ2=sQuery(id+"F0.wireOp",EDGE,"E1");var subQ4=sQuery(id+"F0.wireOp",EDGE,"E0.top");var subQ6=sQuery(id+"F0.wireOp",EDGE,"E0.left");Q0=makeQuery(id+"F3.boolean.opBoolean","SPLIT",FACE,{"disambiguationData":[TD([makeQuery(id+"F1.opExtrude","SWEPT_FACE",FACE,{"disambiguationData":[OSD([subQ6])]})])],"derivedFrom":makeQuery(id+"F1.opExtrude","CAP_FACE",FACE,{"disambiguationData":[OSD([subQ1,subQ4,subQ6,subQ0,subQ2])],"isStart":false})});}
            var sketch = newSketch(context, id + "F4", { "sketchPlane" : qUnion([Q0])});
            skCircle(sketch, "E722", {"center": v(0, 0) * mm, "radius": 40 * mm});
            skCircle(sketch, "E723", {"center": v(0, 0) * mm, "radius": 44.72 * mm});
            skSolve(sketch);
        }
        {
            var Q0;
            {var subQ1=sQuery(id+"F0.wireOp",EDGE,"E0.right");var subQ2=sQuery(id+"F0.wireOp",EDGE,"E0.top");var subQ3=makeQuery(id+"F1.opExtrude","CAP_EDGE",EDGE,{"disambiguationData":[OSD([subQ2]),TDD([makeQuery(id+"F0.imprint","IMPRINT",EDGE,{"disambiguationData":[TD([[makeQuery(id+"F0.imprint","INTERSECT",VERTEX,{"derivedFrom":[subQ2,subQ1]}),1.0]])],"derivedFrom":subQ2})])],"isStart":false});Q0=makeQuery(id+"F4.imprint","IMPRINT",FACE,{"disambiguationData":[TD([[makeQuery(id+"F4.imprint","IMPRINT",EDGE,{"derivedFrom":subQ3}),1.0]])]});}
            var Q1;
            {var subQ1=sQuery(id+"F0.wireOp",EDGE,"E0.left");var subQ2=sQuery(id+"F0.wireOp",EDGE,"E0.bottom");var subQ3=makeQuery(id+"F1.opExtrude","CAP_EDGE",EDGE,{"disambiguationData":[OSD([subQ2]),TDD([makeQuery(id+"F0.imprint","IMPRINT",EDGE,{"disambiguationData":[TD([[makeQuery(id+"F0.imprint","INTERSECT",VERTEX,{"derivedFrom":[subQ2,subQ1]}),-1.0]])],"derivedFrom":subQ2})])],"isStart":false});Q1=makeQuery(id+"F4.imprint","IMPRINT",FACE,{"disambiguationData":[TD([[makeQuery(id+"F4.imprint","IMPRINT",EDGE,{"derivedFrom":subQ3}),-1.0]])]});}
            var Q2;
            {var subQ1=sQuery(id+"F0.wireOp",EDGE,"E0.left");var subQ2=sQuery(id+"F0.wireOp",EDGE,"E0.top");var subQ3=makeQuery(id+"F1.opExtrude","CAP_EDGE",EDGE,{"disambiguationData":[OSD([subQ2]),TDD([makeQuery(id+"F0.imprint","IMPRINT",EDGE,{"disambiguationData":[TD([[makeQuery(id+"F0.imprint","INTERSECT",VERTEX,{"derivedFrom":[subQ2,subQ1]}),-1.0]])],"derivedFrom":subQ2})])],"isStart":false});Q2=makeQuery(id+"F4.imprint","IMPRINT",FACE,{"disambiguationData":[TD([[makeQuery(id+"F4.imprint","IMPRINT",EDGE,{"derivedFrom":subQ3}),1.0]])]});}
            var Q3;
            {var subQ1=sQuery(id+"F0.wireOp",EDGE,"E0.right");var subQ2=sQuery(id+"F0.wireOp",EDGE,"E0.bottom");var subQ3=makeQuery(id+"F1.opExtrude","CAP_EDGE",EDGE,{"disambiguationData":[OSD([subQ2]),TDD([makeQuery(id+"F0.imprint","IMPRINT",EDGE,{"disambiguationData":[TD([[makeQuery(id+"F0.imprint","INTERSECT",VERTEX,{"derivedFrom":[subQ2,subQ1]}),1.0]])],"derivedFrom":subQ2})])],"isStart":false});Q3=makeQuery(id+"F4.imprint","IMPRINT",FACE,{"disambiguationData":[TD([[makeQuery(id+"F4.imprint","IMPRINT",EDGE,{"derivedFrom":subQ3}),-1.0]])]});}
            extrude(context, id + "F5", {"entities" : qUnion([Q0, Q1, Q2, Q3]), "operationType" : NewBodyOperationType.REMOVE, "oppositeDirection" : true, "depth" : 25 * mm, "offsetDistance" : 25 * mm});
        }
    });
